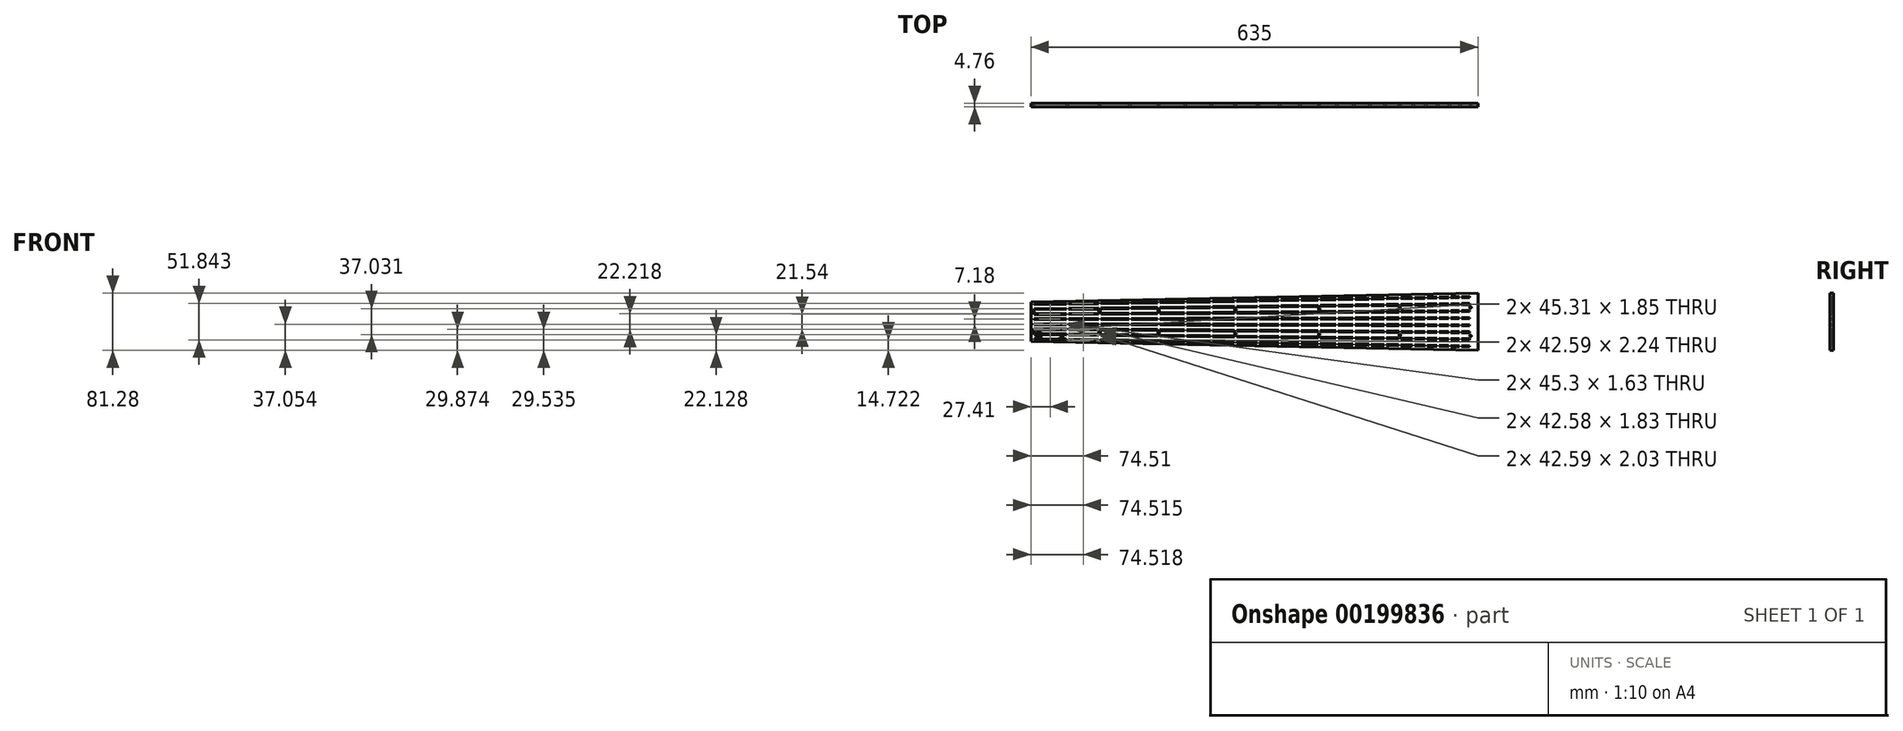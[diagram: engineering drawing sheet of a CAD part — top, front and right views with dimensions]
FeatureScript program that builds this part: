
annotation { "Feature Type Name" : "Feature", "Feature Type Description" : "" }
export const myFeature = defineFeature(function(context is Context, id is Id, definition is map)
    precondition{}
    {
        {
            var Q0;
            Q0=qCreatedBy(makeId("Front.planeOp"),FACE);
            var sketch = newSketch(context, id + "F0", { "sketchPlane" : qUnion([Q0])});
            skLineSegment(sketch, "E0", {"start": v(0, 3.52) * mm, "end": v(648.16, -7.37) * mm, "construction": true});
            skLineSegment(sketch, "E1", {"start": v(0, 4.29) * mm, "end": v(642.9, -6.52) * mm, "construction": true});
            skLineSegment(sketch, "E2", {"start": v(4.76, 3.44) * mm, "end": v(4.77, 4.2) * mm});
            skLineSegment(sketch, "E3", {"start": v(4.77, 4.2) * mm, "end": v(50.06, 3.45) * mm});
            skLineSegment(sketch, "E4", {"start": v(50.06, 3.45) * mm, "end": v(50.05, 2.68) * mm});
            skLineSegment(sketch, "E5", {"start": v(53.23, 2.63) * mm, "end": v(53.24, 3.4) * mm});
            skLineSegment(sketch, "E6", {"start": v(53.24, 3.4) * mm, "end": v(95.8, 2.68) * mm});
            skLineSegment(sketch, "E7", {"start": v(95.8, 2.68) * mm, "end": v(95.8, 1.91) * mm});
            skLineSegment(sketch, "E8", {"start": v(98.97, 1.86) * mm, "end": v(98.98, 2.62) * mm});
            skLineSegment(sketch, "E9", {"start": v(98.98, 2.62) * mm, "end": v(138.98, 1.95) * mm});
            skLineSegment(sketch, "E10", {"start": v(138.98, 1.95) * mm, "end": v(138.97, 1.19) * mm});
            skLineSegment(sketch, "E11", {"start": v(142.14, 1.14) * mm, "end": v(142.16, 1.9) * mm});
            skLineSegment(sketch, "E12", {"start": v(142.16, 1.9) * mm, "end": v(179.73, 1.27) * mm});
            skLineSegment(sketch, "E13", {"start": v(179.73, 1.27) * mm, "end": v(179.72, 0.5) * mm});
            skLineSegment(sketch, "E14", {"start": v(182.89, 0.45) * mm, "end": v(182.9, 1.21) * mm});
            skLineSegment(sketch, "E15", {"start": v(182.9, 1.21) * mm, "end": v(218.2, 0.62) * mm, "construction": true});
            skLineSegment(sketch, "E16", {"start": v(218.2, 0.62) * mm, "end": v(218.19, -0.14) * mm});
            skLineSegment(sketch, "E17", {"start": v(221.36, -0.2) * mm, "end": v(221.38, 0.57) * mm});
            skLineSegment(sketch, "E18", {"start": v(221.38, 0.57) * mm, "end": v(254.5, 0.01) * mm});
            skLineSegment(sketch, "E19", {"start": v(254.5, 0.01) * mm, "end": v(254.5, -0.75) * mm});
            skLineSegment(sketch, "E20", {"start": v(257.67, -0.8) * mm, "end": v(257.68, -0.04) * mm});
            skLineSegment(sketch, "E21", {"start": v(257.68, -0.04) * mm, "end": v(288.78, -0.57) * mm});
            skLineSegment(sketch, "E22", {"start": v(288.78, -0.57) * mm, "end": v(288.76, -1.33) * mm});
            skLineSegment(sketch, "E23", {"start": v(291.94, -1.38) * mm, "end": v(291.95, -0.62) * mm});
            skLineSegment(sketch, "E24", {"start": v(291.95, -0.62) * mm, "end": v(321.12, -1.1) * mm});
            skLineSegment(sketch, "E25", {"start": v(321.12, -1.1) * mm, "end": v(321.1, -1.87) * mm});
            skLineSegment(sketch, "E26", {"start": v(324.28, -1.92) * mm, "end": v(324.3, -1.16) * mm});
            skLineSegment(sketch, "E27", {"start": v(324.3, -1.16) * mm, "end": v(351.65, -1.62) * mm});
            skLineSegment(sketch, "E28", {"start": v(351.65, -1.62) * mm, "end": v(351.64, -2.38) * mm});
            skLineSegment(sketch, "E29", {"start": v(182.9, 1.21) * mm, "end": v(218.2, 0.62) * mm});
            skLineSegment(sketch, "E30", {"start": v(354.81, -2.44) * mm, "end": v(354.83, -1.68) * mm});
            skLineSegment(sketch, "E31", {"start": v(354.83, -1.68) * mm, "end": v(380.47, -2.1) * mm});
            skLineSegment(sketch, "E32", {"start": v(380.47, -2.1) * mm, "end": v(380.45, -2.87) * mm});
            skLineSegment(sketch, "E33", {"start": v(383.63, -2.92) * mm, "end": v(383.64, -2.16) * mm});
            skLineSegment(sketch, "E34", {"start": v(383.64, -2.16) * mm, "end": v(407.67, -2.56) * mm});
            skLineSegment(sketch, "E35", {"start": v(407.67, -2.56) * mm, "end": v(407.65, -3.33) * mm});
            skLineSegment(sketch, "E36", {"start": v(410.83, -3.38) * mm, "end": v(410.84, -2.62) * mm});
            skLineSegment(sketch, "E37", {"start": v(410.84, -2.62) * mm, "end": v(433.34, -3) * mm});
            skLineSegment(sketch, "E38", {"start": v(433.34, -3) * mm, "end": v(433.33, -3.76) * mm});
            skLineSegment(sketch, "E39", {"start": v(436.5, -3.8) * mm, "end": v(436.51, -3.05) * mm});
            skLineSegment(sketch, "E40", {"start": v(436.51, -3.05) * mm, "end": v(457.57, -3.4) * mm});
            skLineSegment(sketch, "E41", {"start": v(457.57, -3.4) * mm, "end": v(457.56, -4.16) * mm});
            skLineSegment(sketch, "E42", {"start": v(460.73, -4.22) * mm, "end": v(460.75, -3.46) * mm});
            skLineSegment(sketch, "E43", {"start": v(460.75, -3.46) * mm, "end": v(480.44, -3.79) * mm});
            skLineSegment(sketch, "E44", {"start": v(480.44, -3.79) * mm, "end": v(480.43, -4.55) * mm});
            skLineSegment(sketch, "E45", {"start": v(483.6, -4.6) * mm, "end": v(483.62, -3.84) * mm});
            skLineSegment(sketch, "E46", {"start": v(483.62, -3.84) * mm, "end": v(502.03, -4.15) * mm});
            skLineSegment(sketch, "E47", {"start": v(502.03, -4.15) * mm, "end": v(502.02, -4.91) * mm});
            skLineSegment(sketch, "E48", {"start": v(505.2, -4.96) * mm, "end": v(505.2, -4.2) * mm});
            skLineSegment(sketch, "E49", {"start": v(505.2, -4.2) * mm, "end": v(522.4, -4.5) * mm});
            skLineSegment(sketch, "E50", {"start": v(522.4, -4.5) * mm, "end": v(522.4, -5.25) * mm});
            skLineSegment(sketch, "E51", {"start": v(525.57, -5.3) * mm, "end": v(525.58, -4.54) * mm});
            skLineSegment(sketch, "E52", {"start": v(525.58, -4.54) * mm, "end": v(541.64, -4.81) * mm});
            skLineSegment(sketch, "E53", {"start": v(541.64, -4.81) * mm, "end": v(541.63, -5.58) * mm});
            skLineSegment(sketch, "E54", {"start": v(544.8, -5.63) * mm, "end": v(544.81, -4.87) * mm});
            skLineSegment(sketch, "E55", {"start": v(544.81, -4.87) * mm, "end": v(559.8, -5.12) * mm});
            skLineSegment(sketch, "E56", {"start": v(559.8, -5.12) * mm, "end": v(559.78, -5.88) * mm});
            skLineSegment(sketch, "E57", {"start": v(562.95, -5.93) * mm, "end": v(562.97, -5.17) * mm});
            skLineSegment(sketch, "E58", {"start": v(562.97, -5.17) * mm, "end": v(576.93, -5.4) * mm});
            skLineSegment(sketch, "E59", {"start": v(576.93, -5.4) * mm, "end": v(576.91, -6.17) * mm});
            skLineSegment(sketch, "E60", {"start": v(580.09, -6.22) * mm, "end": v(580.1, -5.46) * mm});
            skLineSegment(sketch, "E61", {"start": v(580.1, -5.46) * mm, "end": v(593.1, -5.68) * mm});
            skLineSegment(sketch, "E62", {"start": v(593.1, -5.68) * mm, "end": v(593.09, -6.44) * mm});
            skLineSegment(sketch, "E63", {"start": v(596.26, -6.5) * mm, "end": v(596.27, -5.73) * mm});
            skLineSegment(sketch, "E64", {"start": v(596.27, -5.73) * mm, "end": v(608.36, -5.94) * mm});
            skLineSegment(sketch, "E65", {"start": v(608.36, -5.94) * mm, "end": v(608.35, -6.7) * mm});
            skLineSegment(sketch, "E66", {"start": v(611.53, -6.75) * mm, "end": v(611.54, -5.99) * mm});
            skLineSegment(sketch, "E67", {"start": v(611.54, -5.99) * mm, "end": v(622.77, -6.18) * mm});
            skLineSegment(sketch, "E68", {"start": v(622.77, -6.18) * mm, "end": v(622.76, -6.94) * mm});
            skLineSegment(sketch, "E69.MirrorCS", {"start": v(182.89, 0.45) * mm, "end": v(182.88, -0.31) * mm});
            skLineSegment(sketch, "E70.MirrorCS", {"start": v(608.34, -7.46) * mm, "end": v(608.35, -6.7) * mm});
            skLineSegment(sketch, "E71.MirrorCS", {"start": v(221.36, -0.2) * mm, "end": v(221.35, -0.96) * mm});
            skLineSegment(sketch, "E72.MirrorCS", {"start": v(559.77, -6.64) * mm, "end": v(559.78, -5.88) * mm});
            skLineSegment(sketch, "E73.MirrorCS", {"start": v(218.18, -0.9) * mm, "end": v(218.19, -0.14) * mm});
            skLineSegment(sketch, "E74.MirrorCS", {"start": v(291.94, -1.38) * mm, "end": v(291.92, -2.14) * mm});
            skLineSegment(sketch, "E75.MirrorCS", {"start": v(95.78, 1.15) * mm, "end": v(95.8, 1.91) * mm});
            skLineSegment(sketch, "E76.MirrorCS", {"start": v(50.04, 1.92) * mm, "end": v(50.05, 2.68) * mm});
            skLineSegment(sketch, "E77.MirrorCS", {"start": v(611.53, -6.75) * mm, "end": v(611.51, -7.51) * mm});
            skLineSegment(sketch, "E78.MirrorCS", {"start": v(596.26, -6.5) * mm, "end": v(596.25, -7.26) * mm});
            skLineSegment(sketch, "E79.MirrorCS", {"start": v(324.28, -1.92) * mm, "end": v(324.27, -2.69) * mm});
            skLineSegment(sketch, "E80.MirrorCS", {"start": v(580.09, -6.22) * mm, "end": v(580.08, -6.98) * mm});
            skLineSegment(sketch, "E81.MirrorCS", {"start": v(480.42, -5.3) * mm, "end": v(480.43, -4.55) * mm});
            skLineSegment(sketch, "E82.MirrorCS", {"start": v(407.64, -4.09) * mm, "end": v(407.65, -3.33) * mm});
            skLineSegment(sketch, "E83.MirrorCS", {"start": v(593.07, -7.2) * mm, "end": v(593.09, -6.44) * mm});
            skLineSegment(sketch, "E84.MirrorCS", {"start": v(483.6, -4.6) * mm, "end": v(483.6, -5.36) * mm});
            skLineSegment(sketch, "E85.MirrorCS", {"start": v(580.08, -6.98) * mm, "end": v(593.07, -7.2) * mm});
            skLineSegment(sketch, "E86.MirrorCS", {"start": v(522.38, -6.01) * mm, "end": v(522.4, -5.25) * mm});
            skLineSegment(sketch, "E87.MirrorCS", {"start": v(321.1, -2.63) * mm, "end": v(321.1, -1.87) * mm});
            skLineSegment(sketch, "E88.MirrorCS", {"start": v(457.55, -4.93) * mm, "end": v(457.56, -4.16) * mm});
            skLineSegment(sketch, "E89.MirrorCS", {"start": v(562.95, -5.93) * mm, "end": v(562.94, -6.7) * mm});
            skLineSegment(sketch, "E90.MirrorCS", {"start": v(383.63, -2.92) * mm, "end": v(383.62, -3.68) * mm});
            skLineSegment(sketch, "E91.MirrorCS", {"start": v(380.44, -3.63) * mm, "end": v(380.45, -2.87) * mm});
            skLineSegment(sketch, "E92.MirrorCS", {"start": v(505.2, -4.96) * mm, "end": v(505.18, -5.73) * mm});
            skLineSegment(sketch, "E93.MirrorCS", {"start": v(596.25, -7.26) * mm, "end": v(608.34, -7.46) * mm});
            skLineSegment(sketch, "E94.MirrorCS", {"start": v(544.79, -6.4) * mm, "end": v(559.77, -6.64) * mm});
            skLineSegment(sketch, "E95.MirrorCS", {"start": v(142.14, 1.14) * mm, "end": v(142.13, 0.37) * mm});
            skLineSegment(sketch, "E96.MirrorCS", {"start": v(138.96, 0.43) * mm, "end": v(138.97, 1.19) * mm});
            skLineSegment(sketch, "E97.MirrorCS", {"start": v(98.97, 1.86) * mm, "end": v(98.96, 1.1) * mm});
            skLineSegment(sketch, "E98.MirrorCS", {"start": v(53.23, 2.63) * mm, "end": v(53.21, 1.87) * mm});
            skLineSegment(sketch, "E99.MirrorCS", {"start": v(4.76, 3.44) * mm, "end": v(4.75, 2.68) * mm});
            skLineSegment(sketch, "E100.MirrorCS", {"start": v(179.7, -0.26) * mm, "end": v(179.72, 0.5) * mm});
            skLineSegment(sketch, "E101.MirrorCS", {"start": v(433.31, -4.52) * mm, "end": v(433.33, -3.76) * mm});
            skLineSegment(sketch, "E102.MirrorCS", {"start": v(544.8, -5.63) * mm, "end": v(544.79, -6.4) * mm});
            skLineSegment(sketch, "E103.MirrorCS", {"start": v(502, -5.67) * mm, "end": v(502.02, -4.91) * mm});
            skLineSegment(sketch, "E104.MirrorCS", {"start": v(288.75, -2.09) * mm, "end": v(288.76, -1.33) * mm});
            skLineSegment(sketch, "E105.MirrorCS", {"start": v(562.94, -6.7) * mm, "end": v(576.9, -6.93) * mm});
            skLineSegment(sketch, "E106.MirrorCS", {"start": v(254.48, -1.51) * mm, "end": v(254.5, -0.75) * mm});
            skLineSegment(sketch, "E107.MirrorCS", {"start": v(611.51, -7.51) * mm, "end": v(622.75, -7.7) * mm});
            skLineSegment(sketch, "E108.MirrorCS", {"start": v(525.57, -5.3) * mm, "end": v(525.56, -6.07) * mm});
            skLineSegment(sketch, "E109.MirrorCS", {"start": v(351.63, -3.15) * mm, "end": v(351.64, -2.38) * mm});
            skLineSegment(sketch, "E110.MirrorCS", {"start": v(410.83, -3.38) * mm, "end": v(410.82, -4.14) * mm});
            skLineSegment(sketch, "E111.MirrorCS", {"start": v(576.9, -6.93) * mm, "end": v(576.91, -6.17) * mm});
            skLineSegment(sketch, "E112.MirrorCS", {"start": v(257.67, -0.8) * mm, "end": v(257.66, -1.57) * mm});
            skLineSegment(sketch, "E113.MirrorCS", {"start": v(622.75, -7.7) * mm, "end": v(622.76, -6.94) * mm});
            skLineSegment(sketch, "E114.MirrorCS", {"start": v(354.81, -2.44) * mm, "end": v(354.8, -3.2) * mm});
            skLineSegment(sketch, "E115.MirrorCS", {"start": v(505.18, -5.73) * mm, "end": v(522.38, -6.01) * mm});
            skLineSegment(sketch, "E116.MirrorCS", {"start": v(436.5, -3.8) * mm, "end": v(436.49, -4.57) * mm});
            skLineSegment(sketch, "E117.MirrorCS", {"start": v(182.88, -0.31) * mm, "end": v(218.18, -0.9) * mm, "construction": true});
            skLineSegment(sketch, "E118.MirrorCS", {"start": v(460.73, -4.22) * mm, "end": v(460.72, -4.98) * mm});
            skLineSegment(sketch, "E119.MirrorCS", {"start": v(541.61, -6.34) * mm, "end": v(541.63, -5.58) * mm});
            skLineSegment(sketch, "E120.MirrorCS", {"start": v(525.56, -6.07) * mm, "end": v(541.61, -6.34) * mm});
            skLineSegment(sketch, "E121.MirrorCS", {"start": v(221.35, -0.96) * mm, "end": v(254.48, -1.51) * mm});
            skLineSegment(sketch, "E122.MirrorCS", {"start": v(383.62, -3.68) * mm, "end": v(407.64, -4.09) * mm});
            skLineSegment(sketch, "E123.MirrorCS", {"start": v(291.92, -2.14) * mm, "end": v(321.1, -2.63) * mm});
            skLineSegment(sketch, "E124.MirrorCS", {"start": v(436.49, -4.57) * mm, "end": v(457.55, -4.93) * mm});
            skLineSegment(sketch, "E125.MirrorCS", {"start": v(142.13, 0.37) * mm, "end": v(179.7, -0.26) * mm});
            skLineSegment(sketch, "E126.MirrorCS", {"start": v(53.21, 1.87) * mm, "end": v(95.78, 1.15) * mm});
            skLineSegment(sketch, "E127.MirrorCS", {"start": v(4.75, 2.68) * mm, "end": v(50.04, 1.92) * mm});
            skLineSegment(sketch, "E128.MirrorCS", {"start": v(354.8, -3.2) * mm, "end": v(380.44, -3.63) * mm});
            skLineSegment(sketch, "E129.MirrorCS", {"start": v(257.66, -1.57) * mm, "end": v(288.75, -2.09) * mm});
            skLineSegment(sketch, "E130.MirrorCS", {"start": v(483.6, -5.36) * mm, "end": v(502, -5.67) * mm});
            skLineSegment(sketch, "E131.MirrorCS", {"start": v(410.82, -4.14) * mm, "end": v(433.31, -4.52) * mm});
            skLineSegment(sketch, "E132.MirrorCS", {"start": v(182.88, -0.31) * mm, "end": v(218.18, -0.9) * mm});
            skLineSegment(sketch, "E133.MirrorCS", {"start": v(460.72, -4.98) * mm, "end": v(480.42, -5.3) * mm});
            skLineSegment(sketch, "E134.MirrorCS", {"start": v(324.27, -2.69) * mm, "end": v(351.63, -3.15) * mm});
            skLineSegment(sketch, "E135.MirrorCS", {"start": v(98.96, 1.1) * mm, "end": v(138.96, 0.43) * mm});
            skLineSegment(sketch, "E136", {"start": v(-33.04, 0) * mm, "end": v(118.54, 0) * mm, "construction": true});
            skLineSegment(sketch, "E137", {"start": v(0, 10.57) * mm, "end": v(648.2, 2.8) * mm, "construction": true});
            skLineSegment(sketch, "E138", {"start": v(0, 11.33) * mm, "end": v(642.94, 3.62) * mm, "construction": true});
            skLineSegment(sketch, "E139", {"start": v(4.76, 10.52) * mm, "end": v(4.77, 11.28) * mm});
            skLineSegment(sketch, "E140", {"start": v(4.77, 11.28) * mm, "end": v(50.06, 10.73) * mm});
            skLineSegment(sketch, "E141", {"start": v(50.06, 10.73) * mm, "end": v(50.05, 9.97) * mm});
            skLineSegment(sketch, "E142", {"start": v(53.23, 9.93) * mm, "end": v(53.24, 10.7) * mm});
            skLineSegment(sketch, "E143", {"start": v(53.24, 10.7) * mm, "end": v(95.8, 10.19) * mm});
            skLineSegment(sketch, "E144", {"start": v(95.8, 10.19) * mm, "end": v(95.8, 9.42) * mm});
            skLineSegment(sketch, "E145", {"start": v(98.97, 9.38) * mm, "end": v(98.98, 10.15) * mm});
            skLineSegment(sketch, "E146", {"start": v(98.98, 10.15) * mm, "end": v(138.99, 9.67) * mm});
            skLineSegment(sketch, "E147", {"start": v(138.99, 9.67) * mm, "end": v(138.98, 8.9) * mm});
            skLineSegment(sketch, "E148", {"start": v(142.15, 8.87) * mm, "end": v(142.16, 9.63) * mm});
            skLineSegment(sketch, "E149", {"start": v(142.16, 9.63) * mm, "end": v(179.74, 9.18) * mm});
            skLineSegment(sketch, "E150", {"start": v(179.74, 9.18) * mm, "end": v(179.73, 8.42) * mm});
            skLineSegment(sketch, "E151", {"start": v(182.9, 8.38) * mm, "end": v(182.91, 9.14) * mm});
            skLineSegment(sketch, "E152", {"start": v(182.91, 9.14) * mm, "end": v(218.21, 8.72) * mm, "construction": true});
            skLineSegment(sketch, "E153", {"start": v(218.21, 8.72) * mm, "end": v(218.2, 7.95) * mm});
            skLineSegment(sketch, "E154", {"start": v(221.38, 7.92) * mm, "end": v(221.39, 8.68) * mm});
            skLineSegment(sketch, "E155", {"start": v(221.39, 8.68) * mm, "end": v(254.52, 8.28) * mm});
            skLineSegment(sketch, "E156", {"start": v(254.52, 8.28) * mm, "end": v(254.51, 7.52) * mm});
            skLineSegment(sketch, "E157", {"start": v(257.69, 7.48) * mm, "end": v(257.7, 8.24) * mm});
            skLineSegment(sketch, "E158", {"start": v(257.7, 8.24) * mm, "end": v(288.8, 7.87) * mm});
            skLineSegment(sketch, "E159", {"start": v(288.8, 7.87) * mm, "end": v(288.78, 7.1) * mm});
            skLineSegment(sketch, "E160", {"start": v(291.96, 7.07) * mm, "end": v(291.97, 7.83) * mm});
            skLineSegment(sketch, "E161", {"start": v(291.97, 7.83) * mm, "end": v(321.14, 7.48) * mm});
            skLineSegment(sketch, "E162", {"start": v(321.14, 7.48) * mm, "end": v(321.13, 6.72) * mm});
            skLineSegment(sketch, "E163", {"start": v(324.3, 6.68) * mm, "end": v(324.31, 7.44) * mm});
            skLineSegment(sketch, "E164", {"start": v(324.31, 7.44) * mm, "end": v(351.67, 7.11) * mm});
            skLineSegment(sketch, "E165", {"start": v(351.67, 7.11) * mm, "end": v(351.66, 6.35) * mm});
            skLineSegment(sketch, "E166", {"start": v(182.91, 9.14) * mm, "end": v(218.21, 8.72) * mm});
            skLineSegment(sketch, "E167", {"start": v(354.84, 6.31) * mm, "end": v(354.85, 7.08) * mm});
            skLineSegment(sketch, "E168", {"start": v(354.85, 7.08) * mm, "end": v(380.5, 6.77) * mm});
            skLineSegment(sketch, "E169", {"start": v(380.5, 6.77) * mm, "end": v(380.48, 6) * mm});
            skLineSegment(sketch, "E170", {"start": v(383.66, 5.97) * mm, "end": v(383.66, 6.73) * mm});
            skLineSegment(sketch, "E171", {"start": v(383.66, 6.73) * mm, "end": v(407.7, 6.44) * mm});
            skLineSegment(sketch, "E172", {"start": v(407.7, 6.44) * mm, "end": v(407.68, 5.68) * mm});
            skLineSegment(sketch, "E173", {"start": v(410.86, 5.64) * mm, "end": v(410.87, 6.4) * mm});
            skLineSegment(sketch, "E174", {"start": v(410.87, 6.4) * mm, "end": v(433.37, 6.13) * mm});
            skLineSegment(sketch, "E175", {"start": v(433.37, 6.13) * mm, "end": v(433.36, 5.37) * mm});
            skLineSegment(sketch, "E176", {"start": v(436.53, 5.33) * mm, "end": v(436.54, 6.1) * mm});
            skLineSegment(sketch, "E177", {"start": v(436.54, 6.1) * mm, "end": v(457.6, 5.84) * mm});
            skLineSegment(sketch, "E178", {"start": v(457.6, 5.84) * mm, "end": v(457.59, 5.08) * mm});
            skLineSegment(sketch, "E179", {"start": v(460.76, 5.04) * mm, "end": v(460.77, 5.8) * mm});
            skLineSegment(sketch, "E180", {"start": v(460.77, 5.8) * mm, "end": v(480.47, 5.57) * mm});
            skLineSegment(sketch, "E181", {"start": v(480.47, 5.57) * mm, "end": v(480.46, 4.8) * mm});
            skLineSegment(sketch, "E182", {"start": v(483.64, 4.77) * mm, "end": v(483.65, 5.53) * mm});
            skLineSegment(sketch, "E183", {"start": v(483.65, 5.53) * mm, "end": v(502.06, 5.3) * mm});
            skLineSegment(sketch, "E184", {"start": v(502.06, 5.3) * mm, "end": v(502.05, 4.55) * mm});
            skLineSegment(sketch, "E185", {"start": v(505.23, 4.5) * mm, "end": v(505.24, 5.27) * mm});
            skLineSegment(sketch, "E186", {"start": v(505.24, 5.27) * mm, "end": v(522.44, 5.07) * mm});
            skLineSegment(sketch, "E187", {"start": v(522.44, 5.07) * mm, "end": v(522.43, 4.3) * mm});
            skLineSegment(sketch, "E188", {"start": v(525.6, 4.27) * mm, "end": v(525.61, 5.03) * mm});
            skLineSegment(sketch, "E189", {"start": v(525.61, 5.03) * mm, "end": v(541.67, 4.83) * mm});
            skLineSegment(sketch, "E190", {"start": v(541.67, 4.83) * mm, "end": v(541.66, 4.07) * mm});
            skLineSegment(sketch, "E191", {"start": v(544.84, 4.03) * mm, "end": v(544.85, 4.8) * mm});
            skLineSegment(sketch, "E192", {"start": v(544.85, 4.8) * mm, "end": v(559.83, 4.62) * mm});
            skLineSegment(sketch, "E193", {"start": v(559.83, 4.62) * mm, "end": v(559.82, 3.85) * mm});
            skLineSegment(sketch, "E194", {"start": v(563, 3.82) * mm, "end": v(563, 4.58) * mm});
            skLineSegment(sketch, "E195", {"start": v(563, 4.58) * mm, "end": v(576.96, 4.41) * mm});
            skLineSegment(sketch, "E196", {"start": v(576.96, 4.41) * mm, "end": v(576.95, 3.65) * mm});
            skLineSegment(sketch, "E197", {"start": v(580.13, 3.61) * mm, "end": v(580.14, 4.37) * mm});
            skLineSegment(sketch, "E198", {"start": v(580.14, 4.37) * mm, "end": v(593.14, 4.22) * mm});
            skLineSegment(sketch, "E199", {"start": v(593.14, 4.22) * mm, "end": v(593.13, 3.45) * mm});
            skLineSegment(sketch, "E200", {"start": v(596.3, 3.42) * mm, "end": v(596.31, 4.18) * mm});
            skLineSegment(sketch, "E201", {"start": v(596.31, 4.18) * mm, "end": v(608.4, 4.03) * mm});
            skLineSegment(sketch, "E202", {"start": v(608.4, 4.03) * mm, "end": v(608.4, 3.27) * mm});
            skLineSegment(sketch, "E203", {"start": v(611.57, 3.23) * mm, "end": v(611.58, 4) * mm});
            skLineSegment(sketch, "E204", {"start": v(611.58, 4) * mm, "end": v(622.81, 3.86) * mm});
            skLineSegment(sketch, "E205", {"start": v(622.81, 3.86) * mm, "end": v(622.8, 3.1) * mm});
            skLineSegment(sketch, "E206.MirrorCS", {"start": v(182.9, 8.38) * mm, "end": v(182.9, 7.62) * mm});
            skLineSegment(sketch, "E207.MirrorCS", {"start": v(608.38, 2.5) * mm, "end": v(608.4, 3.27) * mm});
            skLineSegment(sketch, "E208.MirrorCS", {"start": v(221.38, 7.92) * mm, "end": v(221.37, 7.15) * mm});
            skLineSegment(sketch, "E209.MirrorCS", {"start": v(559.8, 3.1) * mm, "end": v(559.82, 3.85) * mm});
            skLineSegment(sketch, "E210.MirrorCS", {"start": v(218.2, 7.2) * mm, "end": v(218.2, 7.95) * mm});
            skLineSegment(sketch, "E211.MirrorCS", {"start": v(291.96, 7.07) * mm, "end": v(291.95, 6.3) * mm});
            skLineSegment(sketch, "E212.MirrorCS", {"start": v(95.8, 8.66) * mm, "end": v(95.8, 9.42) * mm});
            skLineSegment(sketch, "E213.MirrorCS", {"start": v(50.05, 9.21) * mm, "end": v(50.05, 9.97) * mm});
            skLineSegment(sketch, "E214.MirrorCS", {"start": v(611.57, 3.23) * mm, "end": v(611.56, 2.47) * mm});
            skLineSegment(sketch, "E215.MirrorCS", {"start": v(596.3, 3.42) * mm, "end": v(596.3, 2.65) * mm});
            skLineSegment(sketch, "E216.MirrorCS", {"start": v(324.3, 6.68) * mm, "end": v(324.3, 5.92) * mm});
            skLineSegment(sketch, "E217.MirrorCS", {"start": v(580.13, 3.61) * mm, "end": v(580.12, 2.85) * mm});
            skLineSegment(sketch, "E218.MirrorCS", {"start": v(480.45, 4.05) * mm, "end": v(480.46, 4.8) * mm});
            skLineSegment(sketch, "E219.MirrorCS", {"start": v(407.67, 4.92) * mm, "end": v(407.68, 5.68) * mm});
            skLineSegment(sketch, "E220.MirrorCS", {"start": v(593.12, 2.7) * mm, "end": v(593.13, 3.45) * mm});
            skLineSegment(sketch, "E221.MirrorCS", {"start": v(483.64, 4.77) * mm, "end": v(483.63, 4) * mm});
            skLineSegment(sketch, "E222.MirrorCS", {"start": v(580.12, 2.85) * mm, "end": v(593.12, 2.7) * mm});
            skLineSegment(sketch, "E223.MirrorCS", {"start": v(522.42, 3.54) * mm, "end": v(522.43, 4.3) * mm});
            skLineSegment(sketch, "E224.MirrorCS", {"start": v(321.12, 5.96) * mm, "end": v(321.13, 6.72) * mm});
            skLineSegment(sketch, "E225.MirrorCS", {"start": v(457.58, 4.32) * mm, "end": v(457.59, 5.08) * mm});
            skLineSegment(sketch, "E226.MirrorCS", {"start": v(563, 3.82) * mm, "end": v(562.98, 3.05) * mm});
            skLineSegment(sketch, "E227.MirrorCS", {"start": v(383.66, 5.97) * mm, "end": v(383.65, 5.2) * mm});
            skLineSegment(sketch, "E228.MirrorCS", {"start": v(380.47, 5.24) * mm, "end": v(380.48, 6) * mm});
            skLineSegment(sketch, "E229.MirrorCS", {"start": v(505.23, 4.5) * mm, "end": v(505.22, 3.75) * mm});
            skLineSegment(sketch, "E230.MirrorCS", {"start": v(596.3, 2.65) * mm, "end": v(608.38, 2.5) * mm});
            skLineSegment(sketch, "E231.MirrorCS", {"start": v(544.83, 3.27) * mm, "end": v(559.8, 3.1) * mm});
            skLineSegment(sketch, "E232.MirrorCS", {"start": v(142.15, 8.87) * mm, "end": v(142.15, 8.1) * mm});
            skLineSegment(sketch, "E233.MirrorCS", {"start": v(138.97, 8.14) * mm, "end": v(138.98, 8.9) * mm});
            skLineSegment(sketch, "E234.MirrorCS", {"start": v(98.97, 9.38) * mm, "end": v(98.97, 8.62) * mm});
            skLineSegment(sketch, "E235.MirrorCS", {"start": v(53.23, 9.93) * mm, "end": v(53.22, 9.17) * mm});
            skLineSegment(sketch, "E236.MirrorCS", {"start": v(4.76, 10.52) * mm, "end": v(4.75, 9.75) * mm});
            skLineSegment(sketch, "E237.MirrorCS", {"start": v(179.72, 7.65) * mm, "end": v(179.73, 8.42) * mm});
            skLineSegment(sketch, "E238.MirrorCS", {"start": v(433.35, 4.61) * mm, "end": v(433.36, 5.37) * mm});
            skLineSegment(sketch, "E239.MirrorCS", {"start": v(544.84, 4.03) * mm, "end": v(544.83, 3.27) * mm});
            skLineSegment(sketch, "E240.MirrorCS", {"start": v(502.04, 3.79) * mm, "end": v(502.05, 4.55) * mm});
            skLineSegment(sketch, "E241.MirrorCS", {"start": v(288.77, 6.35) * mm, "end": v(288.78, 7.1) * mm});
            skLineSegment(sketch, "E242.MirrorCS", {"start": v(562.98, 3.05) * mm, "end": v(576.94, 2.89) * mm});
            skLineSegment(sketch, "E243.MirrorCS", {"start": v(254.5, 6.76) * mm, "end": v(254.51, 7.52) * mm});
            skLineSegment(sketch, "E244.MirrorCS", {"start": v(611.56, 2.47) * mm, "end": v(622.8, 2.34) * mm});
            skLineSegment(sketch, "E245.MirrorCS", {"start": v(525.6, 4.27) * mm, "end": v(525.6, 3.5) * mm});
            skLineSegment(sketch, "E246.MirrorCS", {"start": v(351.65, 5.6) * mm, "end": v(351.66, 6.35) * mm});
            skLineSegment(sketch, "E247.MirrorCS", {"start": v(410.86, 5.64) * mm, "end": v(410.85, 4.88) * mm});
            skLineSegment(sketch, "E248.MirrorCS", {"start": v(576.94, 2.89) * mm, "end": v(576.95, 3.65) * mm});
            skLineSegment(sketch, "E249.MirrorCS", {"start": v(257.69, 7.48) * mm, "end": v(257.68, 6.72) * mm});
            skLineSegment(sketch, "E250.MirrorCS", {"start": v(622.8, 2.34) * mm, "end": v(622.8, 3.1) * mm});
            skLineSegment(sketch, "E251.MirrorCS", {"start": v(354.84, 6.31) * mm, "end": v(354.83, 5.55) * mm});
            skLineSegment(sketch, "E252.MirrorCS", {"start": v(505.22, 3.75) * mm, "end": v(522.42, 3.54) * mm});
            skLineSegment(sketch, "E253.MirrorCS", {"start": v(436.53, 5.33) * mm, "end": v(436.52, 4.57) * mm});
            skLineSegment(sketch, "E254.MirrorCS", {"start": v(182.9, 7.62) * mm, "end": v(218.2, 7.2) * mm, "construction": true});
            skLineSegment(sketch, "E255.MirrorCS", {"start": v(460.76, 5.04) * mm, "end": v(460.76, 4.28) * mm});
            skLineSegment(sketch, "E256.MirrorCS", {"start": v(541.65, 3.31) * mm, "end": v(541.66, 4.07) * mm});
            skLineSegment(sketch, "E257.MirrorCS", {"start": v(525.6, 3.5) * mm, "end": v(541.65, 3.31) * mm});
            skLineSegment(sketch, "E258.MirrorCS", {"start": v(221.37, 7.15) * mm, "end": v(254.5, 6.76) * mm});
            skLineSegment(sketch, "E259.MirrorCS", {"start": v(383.65, 5.2) * mm, "end": v(407.67, 4.92) * mm});
            skLineSegment(sketch, "E260.MirrorCS", {"start": v(291.95, 6.3) * mm, "end": v(321.12, 5.96) * mm});
            skLineSegment(sketch, "E261.MirrorCS", {"start": v(436.52, 4.57) * mm, "end": v(457.58, 4.32) * mm});
            skLineSegment(sketch, "E262.MirrorCS", {"start": v(142.15, 8.1) * mm, "end": v(179.72, 7.65) * mm});
            skLineSegment(sketch, "E263.MirrorCS", {"start": v(53.22, 9.17) * mm, "end": v(95.8, 8.66) * mm});
            skLineSegment(sketch, "E264.MirrorCS", {"start": v(4.75, 9.75) * mm, "end": v(50.05, 9.21) * mm});
            skLineSegment(sketch, "E265.MirrorCS", {"start": v(354.83, 5.55) * mm, "end": v(380.47, 5.24) * mm});
            skLineSegment(sketch, "E266.MirrorCS", {"start": v(257.68, 6.72) * mm, "end": v(288.77, 6.35) * mm});
            skLineSegment(sketch, "E267.MirrorCS", {"start": v(483.63, 4) * mm, "end": v(502.04, 3.79) * mm});
            skLineSegment(sketch, "E268.MirrorCS", {"start": v(410.85, 4.88) * mm, "end": v(433.35, 4.61) * mm});
            skLineSegment(sketch, "E269.MirrorCS", {"start": v(182.9, 7.62) * mm, "end": v(218.2, 7.2) * mm});
            skLineSegment(sketch, "E270.MirrorCS", {"start": v(460.76, 4.28) * mm, "end": v(480.45, 4.05) * mm});
            skLineSegment(sketch, "E271.MirrorCS", {"start": v(324.3, 5.92) * mm, "end": v(351.65, 5.6) * mm});
            skLineSegment(sketch, "E272.MirrorCS", {"start": v(98.97, 8.62) * mm, "end": v(138.97, 8.14) * mm});
            skLineSegment(sketch, "E273", {"start": v(0, 17.62) * mm, "end": v(648.23, 12.95) * mm, "construction": true});
            skLineSegment(sketch, "E274", {"start": v(0, 18.38) * mm, "end": v(642.97, 13.75) * mm, "construction": true});
            skLineSegment(sketch, "E275", {"start": v(4.76, 17.59) * mm, "end": v(4.77, 18.35) * mm});
            skLineSegment(sketch, "E276", {"start": v(4.77, 18.35) * mm, "end": v(50.06, 18.02) * mm});
            skLineSegment(sketch, "E277", {"start": v(50.06, 18.02) * mm, "end": v(50.06, 17.26) * mm});
            skLineSegment(sketch, "E278", {"start": v(53.23, 17.24) * mm, "end": v(53.24, 18) * mm});
            skLineSegment(sketch, "E279", {"start": v(53.24, 18) * mm, "end": v(95.81, 17.7) * mm});
            skLineSegment(sketch, "E280", {"start": v(95.81, 17.7) * mm, "end": v(95.8, 16.93) * mm});
            skLineSegment(sketch, "E281", {"start": v(98.98, 16.9) * mm, "end": v(98.99, 17.67) * mm});
            skLineSegment(sketch, "E282", {"start": v(98.99, 17.67) * mm, "end": v(139, 17.38) * mm});
            skLineSegment(sketch, "E283", {"start": v(139, 17.38) * mm, "end": v(138.99, 16.62) * mm});
            skLineSegment(sketch, "E284", {"start": v(142.16, 16.6) * mm, "end": v(142.17, 17.36) * mm});
            skLineSegment(sketch, "E285", {"start": v(142.17, 17.36) * mm, "end": v(179.74, 17.09) * mm});
            skLineSegment(sketch, "E286", {"start": v(179.74, 17.09) * mm, "end": v(179.74, 16.33) * mm});
            skLineSegment(sketch, "E287", {"start": v(182.91, 16.3) * mm, "end": v(182.92, 17.07) * mm});
            skLineSegment(sketch, "E288", {"start": v(182.92, 17.07) * mm, "end": v(218.22, 16.81) * mm, "construction": true});
            skLineSegment(sketch, "E289", {"start": v(218.22, 16.81) * mm, "end": v(218.21, 16.05) * mm});
            skLineSegment(sketch, "E290", {"start": v(221.39, 16.03) * mm, "end": v(221.4, 16.79) * mm});
            skLineSegment(sketch, "E291", {"start": v(221.4, 16.79) * mm, "end": v(254.53, 16.55) * mm});
            skLineSegment(sketch, "E292", {"start": v(254.53, 16.55) * mm, "end": v(254.52, 15.79) * mm});
            skLineSegment(sketch, "E293", {"start": v(257.7, 15.77) * mm, "end": v(257.7, 16.53) * mm});
            skLineSegment(sketch, "E294", {"start": v(257.7, 16.53) * mm, "end": v(288.8, 16.3) * mm});
            skLineSegment(sketch, "E295", {"start": v(288.8, 16.3) * mm, "end": v(288.8, 15.54) * mm});
            skLineSegment(sketch, "E296", {"start": v(291.97, 15.52) * mm, "end": v(291.98, 16.28) * mm});
            skLineSegment(sketch, "E297", {"start": v(291.98, 16.28) * mm, "end": v(321.15, 16.07) * mm});
            skLineSegment(sketch, "E298", {"start": v(321.15, 16.07) * mm, "end": v(321.14, 15.3) * mm});
            skLineSegment(sketch, "E299", {"start": v(324.32, 15.29) * mm, "end": v(324.33, 16.05) * mm});
            skLineSegment(sketch, "E300", {"start": v(324.33, 16.05) * mm, "end": v(351.68, 15.85) * mm});
            skLineSegment(sketch, "E301", {"start": v(351.68, 15.85) * mm, "end": v(351.68, 15.09) * mm});
            skLineSegment(sketch, "E302", {"start": v(182.92, 17.07) * mm, "end": v(218.22, 16.81) * mm});
            skLineSegment(sketch, "E303", {"start": v(354.85, 15.07) * mm, "end": v(354.86, 15.83) * mm});
            skLineSegment(sketch, "E304", {"start": v(354.86, 15.83) * mm, "end": v(380.5, 15.64) * mm});
            skLineSegment(sketch, "E305", {"start": v(380.5, 15.64) * mm, "end": v(380.5, 14.88) * mm});
            skLineSegment(sketch, "E306", {"start": v(383.67, 14.86) * mm, "end": v(383.68, 15.62) * mm});
            skLineSegment(sketch, "E307", {"start": v(383.68, 15.62) * mm, "end": v(407.7, 15.45) * mm});
            skLineSegment(sketch, "E308", {"start": v(407.7, 15.45) * mm, "end": v(407.7, 14.69) * mm});
            skLineSegment(sketch, "E309", {"start": v(410.88, 14.66) * mm, "end": v(410.88, 15.42) * mm});
            skLineSegment(sketch, "E310", {"start": v(410.88, 15.42) * mm, "end": v(433.38, 15.26) * mm});
            skLineSegment(sketch, "E311", {"start": v(433.38, 15.26) * mm, "end": v(433.38, 14.5) * mm});
            skLineSegment(sketch, "E312", {"start": v(436.55, 14.48) * mm, "end": v(436.56, 15.24) * mm});
            skLineSegment(sketch, "E313", {"start": v(436.56, 15.24) * mm, "end": v(457.62, 15.09) * mm});
            skLineSegment(sketch, "E314", {"start": v(457.62, 15.09) * mm, "end": v(457.61, 14.33) * mm});
            skLineSegment(sketch, "E315", {"start": v(460.79, 14.3) * mm, "end": v(460.8, 15.07) * mm});
            skLineSegment(sketch, "E316", {"start": v(460.8, 15.07) * mm, "end": v(480.5, 14.92) * mm});
            skLineSegment(sketch, "E317", {"start": v(480.5, 14.92) * mm, "end": v(480.49, 14.16) * mm});
            skLineSegment(sketch, "E318", {"start": v(483.66, 14.14) * mm, "end": v(483.67, 14.9) * mm});
            skLineSegment(sketch, "E319", {"start": v(483.67, 14.9) * mm, "end": v(502.08, 14.77) * mm});
            skLineSegment(sketch, "E320", {"start": v(502.08, 14.77) * mm, "end": v(502.08, 14) * mm});
            skLineSegment(sketch, "E321", {"start": v(505.25, 13.98) * mm, "end": v(505.26, 14.75) * mm});
            skLineSegment(sketch, "E322", {"start": v(505.26, 14.75) * mm, "end": v(522.46, 14.62) * mm});
            skLineSegment(sketch, "E323", {"start": v(522.46, 14.62) * mm, "end": v(522.45, 13.86) * mm});
            skLineSegment(sketch, "E324", {"start": v(525.63, 13.84) * mm, "end": v(525.63, 14.6) * mm});
            skLineSegment(sketch, "E325", {"start": v(525.63, 14.6) * mm, "end": v(541.7, 14.48) * mm});
            skLineSegment(sketch, "E326", {"start": v(541.7, 14.48) * mm, "end": v(541.69, 13.72) * mm});
            skLineSegment(sketch, "E327", {"start": v(544.86, 13.7) * mm, "end": v(544.87, 14.46) * mm});
            skLineSegment(sketch, "E328", {"start": v(544.87, 14.46) * mm, "end": v(559.85, 14.35) * mm});
            skLineSegment(sketch, "E329", {"start": v(559.85, 14.35) * mm, "end": v(559.84, 13.6) * mm});
            skLineSegment(sketch, "E330", {"start": v(563.02, 13.57) * mm, "end": v(563.03, 14.33) * mm});
            skLineSegment(sketch, "E331", {"start": v(563.03, 14.33) * mm, "end": v(576.99, 14.23) * mm});
            skLineSegment(sketch, "E332", {"start": v(576.99, 14.23) * mm, "end": v(576.98, 13.47) * mm});
            skLineSegment(sketch, "E333", {"start": v(580.16, 13.44) * mm, "end": v(580.16, 14.2) * mm});
            skLineSegment(sketch, "E334", {"start": v(580.16, 14.2) * mm, "end": v(593.16, 14.11) * mm});
            skLineSegment(sketch, "E335", {"start": v(593.16, 14.11) * mm, "end": v(593.16, 13.35) * mm});
            skLineSegment(sketch, "E336", {"start": v(596.33, 13.33) * mm, "end": v(596.34, 14.09) * mm});
            skLineSegment(sketch, "E337", {"start": v(596.34, 14.09) * mm, "end": v(608.43, 14) * mm});
            skLineSegment(sketch, "E338", {"start": v(608.43, 14) * mm, "end": v(608.42, 13.24) * mm});
            skLineSegment(sketch, "E339", {"start": v(611.6, 13.22) * mm, "end": v(611.6, 13.98) * mm});
            skLineSegment(sketch, "E340", {"start": v(611.6, 13.98) * mm, "end": v(622.84, 13.9) * mm});
            skLineSegment(sketch, "E341", {"start": v(622.84, 13.9) * mm, "end": v(622.83, 13.14) * mm});
            skLineSegment(sketch, "E342.MirrorCS", {"start": v(182.91, 16.3) * mm, "end": v(182.9, 15.54) * mm});
            skLineSegment(sketch, "E343.MirrorCS", {"start": v(608.42, 12.48) * mm, "end": v(608.42, 13.24) * mm});
            skLineSegment(sketch, "E344.MirrorCS", {"start": v(221.39, 16.03) * mm, "end": v(221.38, 15.27) * mm});
            skLineSegment(sketch, "E345.MirrorCS", {"start": v(559.84, 12.83) * mm, "end": v(559.84, 13.6) * mm});
            skLineSegment(sketch, "E346.MirrorCS", {"start": v(218.2, 15.29) * mm, "end": v(218.21, 16.05) * mm});
            skLineSegment(sketch, "E347.MirrorCS", {"start": v(291.97, 15.52) * mm, "end": v(291.97, 14.76) * mm});
            skLineSegment(sketch, "E348.MirrorCS", {"start": v(95.8, 16.17) * mm, "end": v(95.8, 16.93) * mm});
            skLineSegment(sketch, "E349.MirrorCS", {"start": v(50.05, 16.5) * mm, "end": v(50.06, 17.26) * mm});
            skLineSegment(sketch, "E350.MirrorCS", {"start": v(611.6, 13.22) * mm, "end": v(611.6, 12.46) * mm});
            skLineSegment(sketch, "E351.MirrorCS", {"start": v(596.33, 13.33) * mm, "end": v(596.32, 12.57) * mm});
            skLineSegment(sketch, "E352.MirrorCS", {"start": v(324.32, 15.29) * mm, "end": v(324.31, 14.52) * mm});
            skLineSegment(sketch, "E353.MirrorCS", {"start": v(580.16, 13.44) * mm, "end": v(580.15, 12.68) * mm});
            skLineSegment(sketch, "E354.MirrorCS", {"start": v(480.48, 13.4) * mm, "end": v(480.49, 14.16) * mm});
            skLineSegment(sketch, "E355.MirrorCS", {"start": v(407.7, 13.92) * mm, "end": v(407.7, 14.69) * mm});
            skLineSegment(sketch, "E356.MirrorCS", {"start": v(593.15, 12.59) * mm, "end": v(593.16, 13.35) * mm});
            skLineSegment(sketch, "E357.MirrorCS", {"start": v(483.66, 14.14) * mm, "end": v(483.65, 13.38) * mm});
            skLineSegment(sketch, "E358.MirrorCS", {"start": v(580.15, 12.68) * mm, "end": v(593.15, 12.59) * mm});
            skLineSegment(sketch, "E359.MirrorCS", {"start": v(522.45, 13.1) * mm, "end": v(522.45, 13.86) * mm});
            skLineSegment(sketch, "E360.MirrorCS", {"start": v(321.14, 14.55) * mm, "end": v(321.14, 15.3) * mm});
            skLineSegment(sketch, "E361.MirrorCS", {"start": v(457.6, 13.56) * mm, "end": v(457.61, 14.33) * mm});
            skLineSegment(sketch, "E362.MirrorCS", {"start": v(563.02, 13.57) * mm, "end": v(563.01, 12.8) * mm});
            skLineSegment(sketch, "E363.MirrorCS", {"start": v(383.67, 14.86) * mm, "end": v(383.67, 14.1) * mm});
            skLineSegment(sketch, "E364.MirrorCS", {"start": v(380.5, 14.12) * mm, "end": v(380.5, 14.88) * mm});
            skLineSegment(sketch, "E365.MirrorCS", {"start": v(505.25, 13.98) * mm, "end": v(505.25, 13.22) * mm});
            skLineSegment(sketch, "E366.MirrorCS", {"start": v(596.32, 12.57) * mm, "end": v(608.42, 12.48) * mm});
            skLineSegment(sketch, "E367.MirrorCS", {"start": v(544.86, 12.94) * mm, "end": v(559.84, 12.83) * mm});
            skLineSegment(sketch, "E368.MirrorCS", {"start": v(142.16, 16.6) * mm, "end": v(142.16, 15.84) * mm});
            skLineSegment(sketch, "E369.MirrorCS", {"start": v(138.98, 15.86) * mm, "end": v(138.99, 16.62) * mm});
            skLineSegment(sketch, "E370.MirrorCS", {"start": v(98.98, 16.9) * mm, "end": v(98.97, 16.15) * mm});
            skLineSegment(sketch, "E371.MirrorCS", {"start": v(53.23, 17.24) * mm, "end": v(53.23, 16.48) * mm});
            skLineSegment(sketch, "E372.MirrorCS", {"start": v(4.76, 17.59) * mm, "end": v(4.76, 16.82) * mm});
            skLineSegment(sketch, "E373.MirrorCS", {"start": v(179.73, 15.57) * mm, "end": v(179.74, 16.33) * mm});
            skLineSegment(sketch, "E374.MirrorCS", {"start": v(433.37, 13.74) * mm, "end": v(433.38, 14.5) * mm});
            skLineSegment(sketch, "E375.MirrorCS", {"start": v(544.86, 13.7) * mm, "end": v(544.86, 12.94) * mm});
            skLineSegment(sketch, "E376.MirrorCS", {"start": v(502.07, 13.24) * mm, "end": v(502.08, 14) * mm});
            skLineSegment(sketch, "E377.MirrorCS", {"start": v(288.8, 14.78) * mm, "end": v(288.8, 15.54) * mm});
            skLineSegment(sketch, "E378.MirrorCS", {"start": v(563.01, 12.8) * mm, "end": v(576.98, 12.7) * mm});
            skLineSegment(sketch, "E379.MirrorCS", {"start": v(254.52, 15.03) * mm, "end": v(254.52, 15.79) * mm});
            skLineSegment(sketch, "E380.MirrorCS", {"start": v(611.6, 12.46) * mm, "end": v(622.83, 12.37) * mm});
            skLineSegment(sketch, "E381.MirrorCS", {"start": v(525.63, 13.84) * mm, "end": v(525.62, 13.07) * mm});
            skLineSegment(sketch, "E382.MirrorCS", {"start": v(351.67, 14.33) * mm, "end": v(351.68, 15.09) * mm});
            skLineSegment(sketch, "E383.MirrorCS", {"start": v(410.88, 14.66) * mm, "end": v(410.87, 13.9) * mm});
            skLineSegment(sketch, "E384.MirrorCS", {"start": v(576.98, 12.7) * mm, "end": v(576.98, 13.47) * mm});
            skLineSegment(sketch, "E385.MirrorCS", {"start": v(257.7, 15.77) * mm, "end": v(257.7, 15) * mm});
            skLineSegment(sketch, "E386.MirrorCS", {"start": v(622.83, 12.37) * mm, "end": v(622.83, 13.14) * mm});
            skLineSegment(sketch, "E387.MirrorCS", {"start": v(354.85, 15.07) * mm, "end": v(354.85, 14.3) * mm});
            skLineSegment(sketch, "E388.MirrorCS", {"start": v(505.25, 13.22) * mm, "end": v(522.45, 13.1) * mm});
            skLineSegment(sketch, "E389.MirrorCS", {"start": v(436.55, 14.48) * mm, "end": v(436.55, 13.72) * mm});
            skLineSegment(sketch, "E390.MirrorCS", {"start": v(182.9, 15.54) * mm, "end": v(218.2, 15.29) * mm, "construction": true});
            skLineSegment(sketch, "E391.MirrorCS", {"start": v(460.79, 14.3) * mm, "end": v(460.78, 13.54) * mm});
            skLineSegment(sketch, "E392.MirrorCS", {"start": v(541.68, 12.96) * mm, "end": v(541.69, 13.72) * mm});
            skLineSegment(sketch, "E393.MirrorCS", {"start": v(525.62, 13.07) * mm, "end": v(541.68, 12.96) * mm});
            skLineSegment(sketch, "E394.MirrorCS", {"start": v(221.38, 15.27) * mm, "end": v(254.52, 15.03) * mm});
            skLineSegment(sketch, "E395.MirrorCS", {"start": v(383.67, 14.1) * mm, "end": v(407.7, 13.92) * mm});
            skLineSegment(sketch, "E396.MirrorCS", {"start": v(291.97, 14.76) * mm, "end": v(321.14, 14.55) * mm});
            skLineSegment(sketch, "E397.MirrorCS", {"start": v(436.55, 13.72) * mm, "end": v(457.6, 13.56) * mm});
            skLineSegment(sketch, "E398.MirrorCS", {"start": v(142.16, 15.84) * mm, "end": v(179.73, 15.57) * mm});
            skLineSegment(sketch, "E399.MirrorCS", {"start": v(53.23, 16.48) * mm, "end": v(95.8, 16.17) * mm});
            skLineSegment(sketch, "E400.MirrorCS", {"start": v(4.76, 16.82) * mm, "end": v(50.05, 16.5) * mm});
            skLineSegment(sketch, "E401.MirrorCS", {"start": v(354.85, 14.3) * mm, "end": v(380.5, 14.12) * mm});
            skLineSegment(sketch, "E402.MirrorCS", {"start": v(257.7, 15) * mm, "end": v(288.8, 14.78) * mm});
            skLineSegment(sketch, "E403.MirrorCS", {"start": v(483.65, 13.38) * mm, "end": v(502.07, 13.24) * mm});
            skLineSegment(sketch, "E404.MirrorCS", {"start": v(410.87, 13.9) * mm, "end": v(433.37, 13.74) * mm});
            skLineSegment(sketch, "E405.MirrorCS", {"start": v(182.9, 15.54) * mm, "end": v(218.2, 15.29) * mm});
            skLineSegment(sketch, "E406.MirrorCS", {"start": v(460.78, 13.54) * mm, "end": v(480.48, 13.4) * mm});
            skLineSegment(sketch, "E407.MirrorCS", {"start": v(324.31, 14.52) * mm, "end": v(351.67, 14.33) * mm});
            skLineSegment(sketch, "E408.MirrorCS", {"start": v(98.97, 16.15) * mm, "end": v(138.98, 15.86) * mm});
            skLineSegment(sketch, "E409", {"start": v(0, 24.67) * mm, "end": v(648.25, 23.11) * mm, "construction": true});
            skLineSegment(sketch, "E410", {"start": v(0, 25.43) * mm, "end": v(642.98, 23.89) * mm, "construction": true});
            skLineSegment(sketch, "E411", {"start": v(4.76, 24.66) * mm, "end": v(4.76, 25.42) * mm});
            skLineSegment(sketch, "E412", {"start": v(4.76, 25.42) * mm, "end": v(50.06, 25.31) * mm});
            skLineSegment(sketch, "E413", {"start": v(50.06, 25.31) * mm, "end": v(50.06, 24.55) * mm});
            skLineSegment(sketch, "E414", {"start": v(53.23, 24.54) * mm, "end": v(53.23, 25.3) * mm});
            skLineSegment(sketch, "E415", {"start": v(53.23, 25.3) * mm, "end": v(95.8, 25.2) * mm});
            skLineSegment(sketch, "E416", {"start": v(95.8, 25.2) * mm, "end": v(95.8, 24.44) * mm});
            skLineSegment(sketch, "E417", {"start": v(98.98, 24.43) * mm, "end": v(98.98, 25.2) * mm});
            skLineSegment(sketch, "E418", {"start": v(98.98, 25.2) * mm, "end": v(139, 25.1) * mm});
            skLineSegment(sketch, "E419", {"start": v(139, 25.1) * mm, "end": v(138.99, 24.34) * mm});
            skLineSegment(sketch, "E420", {"start": v(142.16, 24.33) * mm, "end": v(142.17, 25.1) * mm});
            skLineSegment(sketch, "E421", {"start": v(142.17, 25.1) * mm, "end": v(179.74, 25) * mm});
            skLineSegment(sketch, "E422", {"start": v(179.74, 25) * mm, "end": v(179.74, 24.24) * mm});
            skLineSegment(sketch, "E423", {"start": v(182.91, 24.23) * mm, "end": v(182.92, 25) * mm});
            skLineSegment(sketch, "E424", {"start": v(182.92, 25) * mm, "end": v(218.22, 24.9) * mm, "construction": true});
            skLineSegment(sketch, "E425", {"start": v(218.22, 24.9) * mm, "end": v(218.22, 24.15) * mm});
            skLineSegment(sketch, "E426", {"start": v(221.4, 24.14) * mm, "end": v(221.4, 24.9) * mm});
            skLineSegment(sketch, "E427", {"start": v(221.4, 24.9) * mm, "end": v(254.53, 24.82) * mm});
            skLineSegment(sketch, "E428", {"start": v(254.53, 24.82) * mm, "end": v(254.53, 24.06) * mm});
            skLineSegment(sketch, "E429", {"start": v(257.7, 24.05) * mm, "end": v(257.7, 24.81) * mm});
            skLineSegment(sketch, "E430", {"start": v(257.7, 24.81) * mm, "end": v(288.8, 24.74) * mm});
            skLineSegment(sketch, "E431", {"start": v(288.8, 24.74) * mm, "end": v(288.8, 23.98) * mm});
            skLineSegment(sketch, "E432", {"start": v(291.98, 23.97) * mm, "end": v(291.98, 24.73) * mm});
            skLineSegment(sketch, "E433", {"start": v(291.98, 24.73) * mm, "end": v(321.15, 24.66) * mm});
            skLineSegment(sketch, "E434", {"start": v(321.15, 24.66) * mm, "end": v(321.15, 23.9) * mm});
            skLineSegment(sketch, "E435", {"start": v(324.33, 23.9) * mm, "end": v(324.33, 24.65) * mm});
            skLineSegment(sketch, "E436", {"start": v(324.33, 24.65) * mm, "end": v(351.69, 24.59) * mm});
            skLineSegment(sketch, "E437", {"start": v(351.69, 24.59) * mm, "end": v(351.69, 23.83) * mm});
            skLineSegment(sketch, "E438", {"start": v(182.92, 25) * mm, "end": v(218.22, 24.9) * mm});
            skLineSegment(sketch, "E439", {"start": v(354.86, 23.82) * mm, "end": v(354.86, 24.58) * mm});
            skLineSegment(sketch, "E440", {"start": v(354.86, 24.58) * mm, "end": v(380.5, 24.52) * mm});
            skLineSegment(sketch, "E441", {"start": v(380.5, 24.52) * mm, "end": v(380.5, 23.76) * mm});
            skLineSegment(sketch, "E442", {"start": v(383.68, 23.75) * mm, "end": v(383.68, 24.51) * mm});
            skLineSegment(sketch, "E443", {"start": v(383.68, 24.51) * mm, "end": v(407.71, 24.45) * mm});
            skLineSegment(sketch, "E444", {"start": v(407.71, 24.45) * mm, "end": v(407.7, 23.7) * mm});
            skLineSegment(sketch, "E445", {"start": v(410.88, 23.68) * mm, "end": v(410.89, 24.45) * mm});
            skLineSegment(sketch, "E446", {"start": v(410.89, 24.45) * mm, "end": v(433.39, 24.4) * mm});
            skLineSegment(sketch, "E447", {"start": v(433.39, 24.4) * mm, "end": v(433.39, 23.63) * mm});
            skLineSegment(sketch, "E448", {"start": v(436.56, 23.62) * mm, "end": v(436.56, 24.38) * mm});
            skLineSegment(sketch, "E449", {"start": v(436.56, 24.38) * mm, "end": v(457.62, 24.33) * mm});
            skLineSegment(sketch, "E450", {"start": v(457.62, 24.33) * mm, "end": v(457.62, 23.57) * mm});
            skLineSegment(sketch, "E451", {"start": v(460.8, 23.56) * mm, "end": v(460.8, 24.33) * mm});
            skLineSegment(sketch, "E452", {"start": v(460.8, 24.33) * mm, "end": v(480.5, 24.28) * mm});
            skLineSegment(sketch, "E453", {"start": v(480.5, 24.28) * mm, "end": v(480.5, 23.52) * mm});
            skLineSegment(sketch, "E454", {"start": v(483.67, 23.5) * mm, "end": v(483.67, 24.27) * mm});
            skLineSegment(sketch, "E455", {"start": v(483.67, 24.27) * mm, "end": v(502.09, 24.23) * mm});
            skLineSegment(sketch, "E456", {"start": v(502.09, 24.23) * mm, "end": v(502.09, 23.46) * mm});
            skLineSegment(sketch, "E457", {"start": v(505.26, 23.46) * mm, "end": v(505.26, 24.22) * mm});
            skLineSegment(sketch, "E458", {"start": v(505.26, 24.22) * mm, "end": v(522.47, 24.18) * mm});
            skLineSegment(sketch, "E459", {"start": v(522.47, 24.18) * mm, "end": v(522.47, 23.42) * mm});
            skLineSegment(sketch, "E460", {"start": v(525.64, 23.4) * mm, "end": v(525.64, 24.17) * mm});
            skLineSegment(sketch, "E461", {"start": v(525.64, 24.17) * mm, "end": v(541.7, 24.13) * mm});
            skLineSegment(sketch, "E462", {"start": v(541.7, 24.13) * mm, "end": v(541.7, 23.37) * mm});
            skLineSegment(sketch, "E463", {"start": v(544.88, 23.36) * mm, "end": v(544.88, 24.12) * mm});
            skLineSegment(sketch, "E464", {"start": v(544.88, 24.12) * mm, "end": v(559.86, 24.09) * mm});
            skLineSegment(sketch, "E465", {"start": v(559.86, 24.09) * mm, "end": v(559.86, 23.33) * mm});
            skLineSegment(sketch, "E466", {"start": v(563.03, 23.32) * mm, "end": v(563.03, 24.08) * mm});
            skLineSegment(sketch, "E467", {"start": v(563.03, 24.08) * mm, "end": v(577, 24.05) * mm});
            skLineSegment(sketch, "E468", {"start": v(577, 24.05) * mm, "end": v(577, 23.29) * mm});
            skLineSegment(sketch, "E469", {"start": v(580.17, 23.28) * mm, "end": v(580.17, 24.04) * mm});
            skLineSegment(sketch, "E470", {"start": v(580.17, 24.04) * mm, "end": v(593.17, 24) * mm});
            skLineSegment(sketch, "E471", {"start": v(593.17, 24) * mm, "end": v(593.17, 23.25) * mm});
            skLineSegment(sketch, "E472", {"start": v(596.34, 23.24) * mm, "end": v(596.35, 24) * mm});
            skLineSegment(sketch, "E473", {"start": v(596.35, 24) * mm, "end": v(608.44, 23.97) * mm});
            skLineSegment(sketch, "E474", {"start": v(608.44, 23.97) * mm, "end": v(608.44, 23.2) * mm});
            skLineSegment(sketch, "E475", {"start": v(611.61, 23.2) * mm, "end": v(611.61, 23.96) * mm});
            skLineSegment(sketch, "E476", {"start": v(611.61, 23.96) * mm, "end": v(622.85, 23.94) * mm});
            skLineSegment(sketch, "E477", {"start": v(622.85, 23.94) * mm, "end": v(622.85, 23.17) * mm});
            skLineSegment(sketch, "E478.MirrorCS", {"start": v(182.91, 24.23) * mm, "end": v(182.91, 23.47) * mm});
            skLineSegment(sketch, "E479.MirrorCS", {"start": v(608.43, 22.45) * mm, "end": v(608.44, 23.2) * mm});
            skLineSegment(sketch, "E480.MirrorCS", {"start": v(221.4, 24.14) * mm, "end": v(221.4, 23.38) * mm});
            skLineSegment(sketch, "E481.MirrorCS", {"start": v(559.86, 22.56) * mm, "end": v(559.86, 23.33) * mm});
            skLineSegment(sketch, "E482.MirrorCS", {"start": v(218.22, 23.38) * mm, "end": v(218.22, 24.15) * mm});
            skLineSegment(sketch, "E483.MirrorCS", {"start": v(291.98, 23.97) * mm, "end": v(291.98, 23.2) * mm});
            skLineSegment(sketch, "E484.MirrorCS", {"start": v(95.8, 23.68) * mm, "end": v(95.8, 24.44) * mm});
            skLineSegment(sketch, "E485.MirrorCS", {"start": v(50.06, 23.79) * mm, "end": v(50.06, 24.55) * mm});
            skLineSegment(sketch, "E486.MirrorCS", {"start": v(611.61, 23.2) * mm, "end": v(611.6, 22.44) * mm});
            skLineSegment(sketch, "E487.MirrorCS", {"start": v(596.34, 23.24) * mm, "end": v(596.34, 22.48) * mm});
            skLineSegment(sketch, "E488.MirrorCS", {"start": v(324.33, 23.9) * mm, "end": v(324.33, 23.13) * mm});
            skLineSegment(sketch, "E489.MirrorCS", {"start": v(580.17, 23.28) * mm, "end": v(580.17, 22.52) * mm});
            skLineSegment(sketch, "E490.MirrorCS", {"start": v(480.5, 22.75) * mm, "end": v(480.5, 23.52) * mm});
            skLineSegment(sketch, "E491.MirrorCS", {"start": v(407.7, 22.93) * mm, "end": v(407.7, 23.7) * mm});
            skLineSegment(sketch, "E492.MirrorCS", {"start": v(593.17, 22.48) * mm, "end": v(593.17, 23.25) * mm});
            skLineSegment(sketch, "E493.MirrorCS", {"start": v(483.67, 23.5) * mm, "end": v(483.67, 22.75) * mm});
            skLineSegment(sketch, "E494.MirrorCS", {"start": v(580.17, 22.52) * mm, "end": v(593.17, 22.48) * mm});
            skLineSegment(sketch, "E495.MirrorCS", {"start": v(522.46, 22.65) * mm, "end": v(522.47, 23.42) * mm});
            skLineSegment(sketch, "E496.MirrorCS", {"start": v(321.15, 23.14) * mm, "end": v(321.15, 23.9) * mm});
            skLineSegment(sketch, "E497.MirrorCS", {"start": v(457.62, 22.8) * mm, "end": v(457.62, 23.57) * mm});
            skLineSegment(sketch, "E498.MirrorCS", {"start": v(563.03, 23.32) * mm, "end": v(563.03, 22.56) * mm});
            skLineSegment(sketch, "E499.MirrorCS", {"start": v(383.68, 23.75) * mm, "end": v(383.68, 22.99) * mm});
            skLineSegment(sketch, "E500.MirrorCS", {"start": v(380.5, 23) * mm, "end": v(380.5, 23.76) * mm});
            skLineSegment(sketch, "E501.MirrorCS", {"start": v(505.26, 23.46) * mm, "end": v(505.26, 22.7) * mm});
            skLineSegment(sketch, "E502.MirrorCS", {"start": v(596.34, 22.48) * mm, "end": v(608.43, 22.45) * mm});
            skLineSegment(sketch, "E503.MirrorCS", {"start": v(544.87, 22.6) * mm, "end": v(559.86, 22.56) * mm});
            skLineSegment(sketch, "E504.MirrorCS", {"start": v(142.16, 24.33) * mm, "end": v(142.16, 23.57) * mm});
            skLineSegment(sketch, "E505.MirrorCS", {"start": v(138.99, 23.57) * mm, "end": v(138.99, 24.34) * mm});
            skLineSegment(sketch, "E506.MirrorCS", {"start": v(98.98, 24.43) * mm, "end": v(98.98, 23.67) * mm});
            skLineSegment(sketch, "E507.MirrorCS", {"start": v(53.23, 24.54) * mm, "end": v(53.23, 23.78) * mm});
            skLineSegment(sketch, "E508.MirrorCS", {"start": v(4.76, 24.66) * mm, "end": v(4.76, 23.9) * mm});
            skLineSegment(sketch, "E509.MirrorCS", {"start": v(179.74, 23.48) * mm, "end": v(179.74, 24.24) * mm});
            skLineSegment(sketch, "E510.MirrorCS", {"start": v(433.38, 22.87) * mm, "end": v(433.39, 23.63) * mm});
            skLineSegment(sketch, "E511.MirrorCS", {"start": v(544.88, 23.36) * mm, "end": v(544.87, 22.6) * mm});
            skLineSegment(sketch, "E512.MirrorCS", {"start": v(502.09, 22.7) * mm, "end": v(502.09, 23.46) * mm});
            skLineSegment(sketch, "E513.MirrorCS", {"start": v(288.8, 23.21) * mm, "end": v(288.8, 23.98) * mm});
            skLineSegment(sketch, "E514.MirrorCS", {"start": v(563.03, 22.56) * mm, "end": v(577, 22.52) * mm});
            skLineSegment(sketch, "E515.MirrorCS", {"start": v(254.53, 23.3) * mm, "end": v(254.53, 24.06) * mm});
            skLineSegment(sketch, "E516.MirrorCS", {"start": v(611.6, 22.44) * mm, "end": v(622.84, 22.41) * mm});
            skLineSegment(sketch, "E517.MirrorCS", {"start": v(525.64, 23.4) * mm, "end": v(525.64, 22.65) * mm});
            skLineSegment(sketch, "E518.MirrorCS", {"start": v(351.68, 23.06) * mm, "end": v(351.69, 23.83) * mm});
            skLineSegment(sketch, "E519.MirrorCS", {"start": v(410.88, 23.68) * mm, "end": v(410.88, 22.92) * mm});
            skLineSegment(sketch, "E520.MirrorCS", {"start": v(577, 22.52) * mm, "end": v(577, 23.29) * mm});
            skLineSegment(sketch, "E521.MirrorCS", {"start": v(257.7, 24.05) * mm, "end": v(257.7, 23.29) * mm});
            skLineSegment(sketch, "E522.MirrorCS", {"start": v(622.84, 22.41) * mm, "end": v(622.85, 23.17) * mm});
            skLineSegment(sketch, "E523.MirrorCS", {"start": v(354.86, 23.82) * mm, "end": v(354.86, 23.06) * mm});
            skLineSegment(sketch, "E524.MirrorCS", {"start": v(505.26, 22.7) * mm, "end": v(522.46, 22.65) * mm});
            skLineSegment(sketch, "E525.MirrorCS", {"start": v(436.56, 23.62) * mm, "end": v(436.56, 22.86) * mm});
            skLineSegment(sketch, "E526.MirrorCS", {"start": v(182.91, 23.47) * mm, "end": v(218.22, 23.38) * mm, "construction": true});
            skLineSegment(sketch, "E527.MirrorCS", {"start": v(460.8, 23.56) * mm, "end": v(460.8, 22.8) * mm});
            skLineSegment(sketch, "E528.MirrorCS", {"start": v(541.7, 22.6) * mm, "end": v(541.7, 23.37) * mm});
            skLineSegment(sketch, "E529.MirrorCS", {"start": v(525.64, 22.65) * mm, "end": v(541.7, 22.6) * mm});
            skLineSegment(sketch, "E530.MirrorCS", {"start": v(221.4, 23.38) * mm, "end": v(254.53, 23.3) * mm});
            skLineSegment(sketch, "E531.MirrorCS", {"start": v(383.68, 22.99) * mm, "end": v(407.7, 22.93) * mm});
            skLineSegment(sketch, "E532.MirrorCS", {"start": v(291.98, 23.2) * mm, "end": v(321.15, 23.14) * mm});
            skLineSegment(sketch, "E533.MirrorCS", {"start": v(436.56, 22.86) * mm, "end": v(457.62, 22.8) * mm});
            skLineSegment(sketch, "E534.MirrorCS", {"start": v(142.16, 23.57) * mm, "end": v(179.74, 23.48) * mm});
            skLineSegment(sketch, "E535.MirrorCS", {"start": v(53.23, 23.78) * mm, "end": v(95.8, 23.68) * mm});
            skLineSegment(sketch, "E536.MirrorCS", {"start": v(4.76, 23.9) * mm, "end": v(50.06, 23.79) * mm});
            skLineSegment(sketch, "E537.MirrorCS", {"start": v(354.86, 23.06) * mm, "end": v(380.5, 23) * mm});
            skLineSegment(sketch, "E538.MirrorCS", {"start": v(257.7, 23.29) * mm, "end": v(288.8, 23.21) * mm});
            skLineSegment(sketch, "E539.MirrorCS", {"start": v(483.67, 22.75) * mm, "end": v(502.09, 22.7) * mm});
            skLineSegment(sketch, "E540.MirrorCS", {"start": v(410.88, 22.92) * mm, "end": v(433.38, 22.87) * mm});
            skLineSegment(sketch, "E541.MirrorCS", {"start": v(182.91, 23.47) * mm, "end": v(218.22, 23.38) * mm});
            skLineSegment(sketch, "E542.MirrorCS", {"start": v(460.8, 22.8) * mm, "end": v(480.5, 22.75) * mm});
            skLineSegment(sketch, "E543.MirrorCS", {"start": v(324.33, 23.13) * mm, "end": v(351.68, 23.06) * mm});
            skLineSegment(sketch, "E544.MirrorCS", {"start": v(98.98, 23.67) * mm, "end": v(138.99, 23.57) * mm});
            skLineSegment(sketch, "E545", {"start": v(0, 28.2) * mm, "end": v(665.02, 28.2) * mm, "construction": true});
            skLineSegment(sketch, "E546.MirrorCS", {"start": v(218.2, 41.1) * mm, "end": v(218.21, 40.34) * mm});
            skLineSegment(sketch, "E547.MirrorCS", {"start": v(218.22, 39.58) * mm, "end": v(218.21, 40.34) * mm});
            skLineSegment(sketch, "E548.MirrorCS", {"start": v(182.91, 40.08) * mm, "end": v(182.92, 39.32) * mm});
            skLineSegment(sketch, "E549.MirrorCS", {"start": v(95.78, 55.24) * mm, "end": v(95.8, 54.47) * mm});
            skLineSegment(sketch, "E550.MirrorCS", {"start": v(50.04, 54.47) * mm, "end": v(50.05, 53.7) * mm});
            skLineSegment(sketch, "E551.MirrorCS", {"start": v(182.91, 40.08) * mm, "end": v(182.9, 40.85) * mm});
            skLineSegment(sketch, "E552.MirrorCS", {"start": v(218.21, 47.67) * mm, "end": v(218.2, 48.43) * mm});
            skLineSegment(sketch, "E553.MirrorCS", {"start": v(351.67, 49.27) * mm, "end": v(351.66, 50.04) * mm});
            skLineSegment(sketch, "E554.MirrorCS", {"start": v(354.84, 50.07) * mm, "end": v(354.85, 49.31) * mm});
            skLineSegment(sketch, "E555.MirrorCS", {"start": v(4.76, 38.8) * mm, "end": v(4.77, 38.04) * mm});
            skLineSegment(sketch, "E556.MirrorCS", {"start": v(324.3, 49.7) * mm, "end": v(324.31, 48.95) * mm});
            skLineSegment(sketch, "E557.MirrorCS", {"start": v(218.2, 49.2) * mm, "end": v(218.2, 48.43) * mm});
            skLineSegment(sketch, "E558.MirrorCS", {"start": v(53.23, 53.76) * mm, "end": v(53.21, 54.52) * mm});
            skLineSegment(sketch, "E559.MirrorCS", {"start": v(98.97, 54.53) * mm, "end": v(98.96, 55.29) * mm});
            skLineSegment(sketch, "E560.MirrorCS", {"start": v(324.32, 41.1) * mm, "end": v(324.31, 41.86) * mm});
            skLineSegment(sketch, "E561.MirrorCS", {"start": v(321.12, 50.43) * mm, "end": v(321.13, 49.67) * mm});
            skLineSegment(sketch, "E562.MirrorCS", {"start": v(541.65, 53.08) * mm, "end": v(541.66, 52.32) * mm});
            skLineSegment(sketch, "E563.MirrorCS", {"start": v(291.96, 49.32) * mm, "end": v(291.97, 48.56) * mm});
            skLineSegment(sketch, "E564.MirrorCS", {"start": v(95.8, 46.2) * mm, "end": v(95.8, 46.96) * mm});
            skLineSegment(sketch, "E565.MirrorCS", {"start": v(410.88, 41.73) * mm, "end": v(410.87, 42.49) * mm});
            skLineSegment(sketch, "E566.MirrorCS", {"start": v(522.42, 52.85) * mm, "end": v(522.43, 52.08) * mm});
            skLineSegment(sketch, "E567.MirrorCS", {"start": v(288.8, 48.52) * mm, "end": v(288.78, 49.28) * mm});
            skLineSegment(sketch, "E568.MirrorCS", {"start": v(544.84, 52.35) * mm, "end": v(544.85, 51.6) * mm});
            skLineSegment(sketch, "E569.MirrorCS", {"start": v(608.38, 53.88) * mm, "end": v(608.4, 53.12) * mm});
            skLineSegment(sketch, "E570.MirrorCS", {"start": v(611.6, 43.17) * mm, "end": v(611.6, 43.93) * mm});
            skLineSegment(sketch, "E571.MirrorCS", {"start": v(541.67, 51.55) * mm, "end": v(541.66, 52.32) * mm});
            skLineSegment(sketch, "E572.MirrorCS", {"start": v(182.9, 48.01) * mm, "end": v(182.9, 48.77) * mm});
            skLineSegment(sketch, "E573.MirrorCS", {"start": v(53.23, 46.45) * mm, "end": v(53.24, 45.7) * mm});
            skLineSegment(sketch, "E574.MirrorCS", {"start": v(182.91, 32.16) * mm, "end": v(182.91, 32.92) * mm});
            skLineSegment(sketch, "E575.MirrorCS", {"start": v(480.5, 41.46) * mm, "end": v(480.49, 42.23) * mm});
            skLineSegment(sketch, "E576.MirrorCS", {"start": v(179.72, 48.73) * mm, "end": v(179.73, 47.97) * mm});
            skLineSegment(sketch, "E577.MirrorCS", {"start": v(257.69, 48.9) * mm, "end": v(257.7, 48.15) * mm});
            skLineSegment(sketch, "E578.MirrorCS", {"start": v(50.06, 45.65) * mm, "end": v(50.05, 46.42) * mm});
            skLineSegment(sketch, "E579.MirrorCS", {"start": v(179.74, 32.91) * mm, "end": v(179.74, 32.15) * mm});
            skLineSegment(sketch, "E580.MirrorCS", {"start": v(50.05, 39.89) * mm, "end": v(50.06, 39.13) * mm});
            skLineSegment(sketch, "E581.MirrorCS", {"start": v(480.45, 52.34) * mm, "end": v(480.46, 51.58) * mm});
            skLineSegment(sketch, "E582.MirrorCS", {"start": v(608.4, 52.35) * mm, "end": v(608.4, 53.12) * mm});
            skLineSegment(sketch, "E583.MirrorCS", {"start": v(522.44, 51.32) * mm, "end": v(522.43, 52.08) * mm});
            skLineSegment(sketch, "E584.MirrorCS", {"start": v(4.76, 45.87) * mm, "end": v(4.77, 45.11) * mm});
            skLineSegment(sketch, "E585.MirrorCS", {"start": v(354.84, 50.07) * mm, "end": v(354.83, 50.84) * mm});
            skLineSegment(sketch, "E586.MirrorCS", {"start": v(53.23, 46.45) * mm, "end": v(53.22, 47.22) * mm});
            skLineSegment(sketch, "E587.MirrorCS", {"start": v(324.32, 41.1) * mm, "end": v(324.33, 40.34) * mm});
            skLineSegment(sketch, "E588.MirrorCS", {"start": v(139, 39) * mm, "end": v(138.99, 39.77) * mm});
            skLineSegment(sketch, "E589.MirrorCS", {"start": v(291.97, 40.87) * mm, "end": v(291.97, 41.63) * mm});
            skLineSegment(sketch, "E590.MirrorCS", {"start": v(4.76, 45.87) * mm, "end": v(4.75, 46.63) * mm});
            skLineSegment(sketch, "E591.MirrorCS", {"start": v(4.76, 52.94) * mm, "end": v(4.77, 52.18) * mm});
            skLineSegment(sketch, "E592.MirrorCS", {"start": v(50.06, 52.94) * mm, "end": v(50.05, 53.7) * mm});
            skLineSegment(sketch, "E593.MirrorCS", {"start": v(53.23, 53.76) * mm, "end": v(53.24, 53) * mm});
            skLineSegment(sketch, "E594.MirrorCS", {"start": v(95.8, 53.71) * mm, "end": v(95.8, 54.47) * mm});
            skLineSegment(sketch, "E595.MirrorCS", {"start": v(98.97, 54.53) * mm, "end": v(98.98, 53.76) * mm});
            skLineSegment(sketch, "E596.MirrorCS", {"start": v(351.65, 50.8) * mm, "end": v(351.66, 50.04) * mm});
            skLineSegment(sketch, "E597.MirrorCS", {"start": v(98.98, 39.48) * mm, "end": v(98.99, 38.72) * mm});
            skLineSegment(sketch, "E598.MirrorCS", {"start": v(179.74, 31.39) * mm, "end": v(179.74, 32.15) * mm});
            skLineSegment(sketch, "E599.MirrorCS", {"start": v(257.69, 48.9) * mm, "end": v(257.68, 49.67) * mm});
            skLineSegment(sketch, "E600.MirrorCS", {"start": v(380.5, 49.62) * mm, "end": v(380.48, 50.38) * mm});
            skLineSegment(sketch, "E601.MirrorCS", {"start": v(257.7, 40.62) * mm, "end": v(257.7, 39.86) * mm});
            skLineSegment(sketch, "E602.MirrorCS", {"start": v(410.88, 41.73) * mm, "end": v(410.88, 40.96) * mm});
            skLineSegment(sketch, "E603.MirrorCS", {"start": v(50.06, 38.37) * mm, "end": v(50.06, 39.13) * mm});
            skLineSegment(sketch, "E604.MirrorCS", {"start": v(480.47, 50.82) * mm, "end": v(480.46, 51.58) * mm});
            skLineSegment(sketch, "E605.MirrorCS", {"start": v(50.05, 47.18) * mm, "end": v(50.05, 46.42) * mm});
            skLineSegment(sketch, "E606.MirrorCS", {"start": v(221.39, 40.36) * mm, "end": v(221.38, 41.12) * mm});
            skLineSegment(sketch, "E607.MirrorCS", {"start": v(291.97, 40.87) * mm, "end": v(291.98, 40.1) * mm});
            skLineSegment(sketch, "E608.MirrorCS", {"start": v(324.3, 49.7) * mm, "end": v(324.3, 50.47) * mm});
            skLineSegment(sketch, "E609.MirrorCS", {"start": v(608.42, 43.9) * mm, "end": v(608.42, 43.15) * mm});
            skLineSegment(sketch, "E610.MirrorCS", {"start": v(182.9, 48.01) * mm, "end": v(182.91, 47.25) * mm});
            skLineSegment(sketch, "E611.MirrorCS", {"start": v(380.47, 51.14) * mm, "end": v(380.48, 50.38) * mm});
            skLineSegment(sketch, "E612.MirrorCS", {"start": v(95.8, 47.73) * mm, "end": v(95.8, 46.96) * mm});
            skLineSegment(sketch, "E613.MirrorCS", {"start": v(4.76, 38.8) * mm, "end": v(4.76, 39.56) * mm});
            skLineSegment(sketch, "E614.MirrorCS", {"start": v(4.76, 52.94) * mm, "end": v(4.75, 53.7) * mm});
            skLineSegment(sketch, "E615.MirrorCS", {"start": v(291.96, 49.32) * mm, "end": v(291.95, 50.08) * mm});
            skLineSegment(sketch, "E616.MirrorCS", {"start": v(53.23, 39.15) * mm, "end": v(53.23, 39.91) * mm});
            skLineSegment(sketch, "E617.MirrorCS", {"start": v(611.6, 43.17) * mm, "end": v(611.6, 42.4) * mm});
            skLineSegment(sketch, "E618.MirrorCS", {"start": v(288.77, 50.04) * mm, "end": v(288.78, 49.28) * mm});
            skLineSegment(sketch, "E619.MirrorCS", {"start": v(321.14, 48.9) * mm, "end": v(321.13, 49.67) * mm});
            skLineSegment(sketch, "E620.MirrorCS", {"start": v(480.48, 42.99) * mm, "end": v(480.49, 42.23) * mm});
            skLineSegment(sketch, "E621.MirrorCS", {"start": v(98.98, 39.48) * mm, "end": v(98.97, 40.24) * mm});
            skLineSegment(sketch, "E622.MirrorCS", {"start": v(221.39, 40.36) * mm, "end": v(221.4, 39.6) * mm});
            skLineSegment(sketch, "E623.MirrorCS", {"start": v(608.43, 42.39) * mm, "end": v(608.42, 43.15) * mm});
            skLineSegment(sketch, "E624.MirrorCS", {"start": v(257.7, 40.62) * mm, "end": v(257.7, 41.38) * mm});
            skLineSegment(sketch, "E625.MirrorCS", {"start": v(138.98, 40.53) * mm, "end": v(138.99, 39.77) * mm});
            skLineSegment(sketch, "E626.MirrorCS", {"start": v(580.09, 62.61) * mm, "end": v(580.08, 63.37) * mm});
            skLineSegment(sketch, "E627.MirrorCS", {"start": v(218.2, 55.77) * mm, "end": v(218.19, 56.53) * mm});
            skLineSegment(sketch, "E628.MirrorCS", {"start": v(95.8, 31.19) * mm, "end": v(95.8, 31.95) * mm});
            skLineSegment(sketch, "E629.MirrorCS", {"start": v(142.16, 39.8) * mm, "end": v(142.16, 40.55) * mm});
            skLineSegment(sketch, "E630.MirrorCS", {"start": v(576.98, 43.68) * mm, "end": v(576.98, 42.92) * mm});
            skLineSegment(sketch, "E631.MirrorCS", {"start": v(502.04, 52.6) * mm, "end": v(502.05, 51.84) * mm});
            skLineSegment(sketch, "E632.MirrorCS", {"start": v(436.53, 51.05) * mm, "end": v(436.54, 50.3) * mm});
            skLineSegment(sketch, "E633.MirrorCS", {"start": v(544.84, 52.35) * mm, "end": v(544.83, 53.12) * mm});
            skLineSegment(sketch, "E634.MirrorCS", {"start": v(460.76, 51.34) * mm, "end": v(460.76, 52.1) * mm});
            skLineSegment(sketch, "E635.MirrorCS", {"start": v(433.37, 50.25) * mm, "end": v(433.36, 51.02) * mm});
            skLineSegment(sketch, "E636.MirrorCS", {"start": v(576.9, 63.32) * mm, "end": v(576.91, 62.56) * mm});
            skLineSegment(sketch, "E637.MirrorCS", {"start": v(179.74, 39.3) * mm, "end": v(179.74, 40.06) * mm});
            skLineSegment(sketch, "E638.MirrorCS", {"start": v(433.35, 51.78) * mm, "end": v(433.36, 51.02) * mm});
            skLineSegment(sketch, "E639.MirrorCS", {"start": v(53.23, 31.85) * mm, "end": v(53.23, 31.08) * mm});
            skLineSegment(sketch, "E640.MirrorCS", {"start": v(483.64, 51.62) * mm, "end": v(483.63, 52.38) * mm});
            skLineSegment(sketch, "E641.MirrorCS", {"start": v(436.53, 51.05) * mm, "end": v(436.52, 51.82) * mm});
            skLineSegment(sketch, "E642.MirrorCS", {"start": v(410.86, 50.75) * mm, "end": v(410.87, 49.98) * mm});
            skLineSegment(sketch, "E643.MirrorCS", {"start": v(50.06, 31.08) * mm, "end": v(50.06, 31.84) * mm});
            skLineSegment(sketch, "E644.MirrorCS", {"start": v(457.6, 42.82) * mm, "end": v(457.61, 42.06) * mm});
            skLineSegment(sketch, "E645.MirrorCS", {"start": v(138.99, 32.81) * mm, "end": v(138.99, 32.05) * mm});
            skLineSegment(sketch, "E646.MirrorCS", {"start": v(383.63, 59.3) * mm, "end": v(383.62, 60.07) * mm});
            skLineSegment(sketch, "E647.MirrorCS", {"start": v(291.94, 57.77) * mm, "end": v(291.92, 58.53) * mm});
            skLineSegment(sketch, "E648.MirrorCS", {"start": v(383.66, 50.42) * mm, "end": v(383.66, 49.66) * mm});
            skLineSegment(sketch, "E649.MirrorCS", {"start": v(98.97, 47) * mm, "end": v(98.97, 47.76) * mm});
            skLineSegment(sketch, "E650.MirrorCS", {"start": v(457.62, 41.3) * mm, "end": v(457.61, 42.06) * mm});
            skLineSegment(sketch, "E651.MirrorCS", {"start": v(563.02, 42.82) * mm, "end": v(563.01, 43.58) * mm});
            skLineSegment(sketch, "E652.MirrorCS", {"start": v(98.98, 31.96) * mm, "end": v(98.98, 32.72) * mm});
            skLineSegment(sketch, "E653.MirrorCS", {"start": v(611.57, 53.15) * mm, "end": v(611.58, 52.4) * mm});
            skLineSegment(sketch, "E654.MirrorCS", {"start": v(254.52, 41.36) * mm, "end": v(254.52, 40.6) * mm});
            skLineSegment(sketch, "E655.MirrorCS", {"start": v(4.76, 31.73) * mm, "end": v(4.76, 30.97) * mm});
            skLineSegment(sketch, "E656.MirrorCS", {"start": v(53.23, 31.85) * mm, "end": v(53.23, 32.6) * mm});
            skLineSegment(sketch, "E657.MirrorCS", {"start": v(525.6, 52.12) * mm, "end": v(525.61, 51.36) * mm});
            skLineSegment(sketch, "E658.MirrorCS", {"start": v(142.16, 39.8) * mm, "end": v(142.17, 39.03) * mm});
            skLineSegment(sketch, "E659.MirrorCS", {"start": v(611.6, 43.93) * mm, "end": v(622.83, 44.01) * mm});
            skLineSegment(sketch, "E660.MirrorCS", {"start": v(95.8, 40.22) * mm, "end": v(95.8, 39.46) * mm});
            skLineSegment(sketch, "E661.MirrorCS", {"start": v(4.76, 31.73) * mm, "end": v(4.76, 32.5) * mm});
            skLineSegment(sketch, "E662.MirrorCS", {"start": v(182.89, 55.94) * mm, "end": v(182.9, 55.17) * mm});
            skLineSegment(sketch, "E663.MirrorCS", {"start": v(53.23, 39.15) * mm, "end": v(53.24, 38.39) * mm});
            skLineSegment(sketch, "E664.MirrorCS", {"start": v(483.64, 51.62) * mm, "end": v(483.65, 50.86) * mm});
            skLineSegment(sketch, "E665.MirrorCS", {"start": v(611.57, 53.15) * mm, "end": v(611.56, 53.92) * mm});
            skLineSegment(sketch, "E666.MirrorCS", {"start": v(179.74, 47.21) * mm, "end": v(179.73, 47.97) * mm});
            skLineSegment(sketch, "E667.MirrorCS", {"start": v(608.34, 63.85) * mm, "end": v(608.35, 63.09) * mm});
            skLineSegment(sketch, "E668.MirrorCS", {"start": v(522.38, 62.4) * mm, "end": v(522.4, 61.64) * mm});
            skLineSegment(sketch, "E669.MirrorCS", {"start": v(525.63, 42.55) * mm, "end": v(525.62, 43.31) * mm});
            skLineSegment(sketch, "E670.MirrorCS", {"start": v(182.89, 55.94) * mm, "end": v(182.88, 56.7) * mm});
            skLineSegment(sketch, "E671.MirrorCS", {"start": v(218.18, 57.3) * mm, "end": v(218.19, 56.53) * mm});
            skLineSegment(sketch, "E672.MirrorCS", {"start": v(179.73, 40.82) * mm, "end": v(179.74, 40.06) * mm});
            skLineSegment(sketch, "E673.MirrorCS", {"start": v(436.55, 41.9) * mm, "end": v(436.55, 42.67) * mm});
            skLineSegment(sketch, "E674.MirrorCS", {"start": v(562.95, 62.32) * mm, "end": v(562.97, 61.56) * mm});
            skLineSegment(sketch, "E675.MirrorCS", {"start": v(622.84, 42.49) * mm, "end": v(622.83, 43.25) * mm});
            skLineSegment(sketch, "E676.MirrorCS", {"start": v(525.6, 52.12) * mm, "end": v(525.6, 52.88) * mm});
            skLineSegment(sketch, "E677.MirrorCS", {"start": v(580.13, 52.78) * mm, "end": v(580.14, 52.02) * mm});
            skLineSegment(sketch, "E678.MirrorCS", {"start": v(142.16, 32.06) * mm, "end": v(142.16, 32.82) * mm});
            skLineSegment(sketch, "E679.MirrorCS", {"start": v(95.81, 38.7) * mm, "end": v(95.8, 39.46) * mm});
            skLineSegment(sketch, "E680.MirrorCS", {"start": v(142.15, 47.52) * mm, "end": v(142.15, 48.28) * mm});
            skLineSegment(sketch, "E681.MirrorCS", {"start": v(576.94, 53.5) * mm, "end": v(576.95, 52.74) * mm});
            skLineSegment(sketch, "E682.MirrorCS", {"start": v(502.06, 51.08) * mm, "end": v(502.05, 51.84) * mm});
            skLineSegment(sketch, "E683.MirrorCS", {"start": v(182.91, 32.16) * mm, "end": v(182.92, 31.4) * mm});
            skLineSegment(sketch, "E684.MirrorCS", {"start": v(522.45, 43.3) * mm, "end": v(522.45, 42.53) * mm});
            skLineSegment(sketch, "E685.MirrorCS", {"start": v(410.86, 50.75) * mm, "end": v(410.85, 51.5) * mm});
            skLineSegment(sketch, "E686.MirrorCS", {"start": v(291.94, 57.77) * mm, "end": v(291.95, 57) * mm});
            skLineSegment(sketch, "E687.MirrorCS", {"start": v(436.5, 60.2) * mm, "end": v(436.51, 59.44) * mm});
            skLineSegment(sketch, "E688.MirrorCS", {"start": v(254.53, 39.84) * mm, "end": v(254.52, 40.6) * mm});
            skLineSegment(sketch, "E689.MirrorCS", {"start": v(407.7, 40.94) * mm, "end": v(407.7, 41.7) * mm});
            skLineSegment(sketch, "E690.MirrorCS", {"start": v(525.63, 42.55) * mm, "end": v(525.63, 41.79) * mm});
            skLineSegment(sketch, "E691.MirrorCS", {"start": v(611.6, 42.4) * mm, "end": v(622.84, 42.49) * mm});
            skLineSegment(sketch, "E692.MirrorCS", {"start": v(576.96, 51.98) * mm, "end": v(576.95, 52.74) * mm});
            skLineSegment(sketch, "E693.MirrorCS", {"start": v(436.5, 60.2) * mm, "end": v(436.49, 60.96) * mm});
            skLineSegment(sketch, "E694.MirrorCS", {"start": v(179.7, 56.65) * mm, "end": v(179.72, 55.88) * mm});
            skLineSegment(sketch, "E695.MirrorCS", {"start": v(142.15, 47.52) * mm, "end": v(142.16, 46.76) * mm});
            skLineSegment(sketch, "E696.MirrorCS", {"start": v(95.8, 32.71) * mm, "end": v(95.8, 31.95) * mm});
            skLineSegment(sketch, "E697.MirrorCS", {"start": v(142.16, 32.06) * mm, "end": v(142.17, 31.3) * mm});
            skLineSegment(sketch, "E698.MirrorCS", {"start": v(383.66, 50.42) * mm, "end": v(383.65, 51.18) * mm});
            skLineSegment(sketch, "E699.MirrorCS", {"start": v(460.76, 51.34) * mm, "end": v(460.77, 50.58) * mm});
            skLineSegment(sketch, "E700.MirrorCS", {"start": v(593.07, 63.6) * mm, "end": v(593.09, 62.83) * mm});
            skLineSegment(sketch, "E701.MirrorCS", {"start": v(139, 31.29) * mm, "end": v(138.99, 32.05) * mm});
            skLineSegment(sketch, "E702.MirrorCS", {"start": v(407.7, 42.46) * mm, "end": v(407.7, 41.7) * mm});
            skLineSegment(sketch, "E703.MirrorCS", {"start": v(522.46, 41.77) * mm, "end": v(522.45, 42.53) * mm});
            skLineSegment(sketch, "E704.MirrorCS", {"start": v(563, 52.57) * mm, "end": v(563, 51.8) * mm});
            skLineSegment(sketch, "E705.MirrorCS", {"start": v(522.4, 60.88) * mm, "end": v(522.4, 61.64) * mm});
            skLineSegment(sketch, "E706.MirrorCS", {"start": v(622.83, 44.01) * mm, "end": v(622.83, 43.25) * mm});
            skLineSegment(sketch, "E707.MirrorCS", {"start": v(98.97, 47) * mm, "end": v(98.98, 46.24) * mm});
            skLineSegment(sketch, "E708.MirrorCS", {"start": v(383.63, 59.3) * mm, "end": v(383.64, 58.55) * mm});
            skLineSegment(sketch, "E709.MirrorCS", {"start": v(608.36, 62.32) * mm, "end": v(608.35, 63.09) * mm});
            skLineSegment(sketch, "E710.MirrorCS", {"start": v(98.98, 31.96) * mm, "end": v(98.98, 31.2) * mm});
            skLineSegment(sketch, "E711.MirrorCS", {"start": v(559.83, 51.77) * mm, "end": v(559.82, 52.53) * mm});
            skLineSegment(sketch, "E712.MirrorCS", {"start": v(559.8, 53.3) * mm, "end": v(559.82, 52.53) * mm});
            skLineSegment(sketch, "E713.MirrorCS", {"start": v(380.47, 58.5) * mm, "end": v(380.45, 59.26) * mm});
            skLineSegment(sketch, "E714.MirrorCS", {"start": v(505.2, 61.35) * mm, "end": v(505.2, 60.6) * mm});
            skLineSegment(sketch, "E715.MirrorCS", {"start": v(596.27, 62.12) * mm, "end": v(608.36, 62.32) * mm});
            skLineSegment(sketch, "E716.MirrorCS", {"start": v(291.98, 32.42) * mm, "end": v(291.98, 31.66) * mm});
            skLineSegment(sketch, "E717.MirrorCS", {"start": v(502.08, 41.62) * mm, "end": v(502.08, 42.38) * mm});
            skLineSegment(sketch, "E718.MirrorCS", {"start": v(596.33, 43.06) * mm, "end": v(596.34, 42.3) * mm});
            skLineSegment(sketch, "E719.MirrorCS", {"start": v(221.38, 48.47) * mm, "end": v(221.37, 49.23) * mm});
            skLineSegment(sketch, "E720.MirrorCS", {"start": v(257.67, 57.2) * mm, "end": v(257.66, 57.95) * mm});
            skLineSegment(sketch, "E721.MirrorCS", {"start": v(596.33, 43.06) * mm, "end": v(596.32, 43.82) * mm});
            skLineSegment(sketch, "E722.MirrorCS", {"start": v(354.85, 41.32) * mm, "end": v(354.86, 40.56) * mm});
            skLineSegment(sketch, "E723.MirrorCS", {"start": v(142.14, 55.25) * mm, "end": v(142.13, 56.01) * mm});
            skLineSegment(sketch, "E724.MirrorCS", {"start": v(502.03, 60.54) * mm, "end": v(502.02, 61.3) * mm});
            skLineSegment(sketch, "E725.MirrorCS", {"start": v(596.26, 62.88) * mm, "end": v(596.27, 62.12) * mm});
            skLineSegment(sketch, "E726.MirrorCS", {"start": v(324.28, 58.31) * mm, "end": v(324.27, 59.07) * mm});
            skLineSegment(sketch, "E727.MirrorCS", {"start": v(596.32, 43.82) * mm, "end": v(608.42, 43.9) * mm});
            skLineSegment(sketch, "E728.MirrorCS", {"start": v(351.67, 42.06) * mm, "end": v(351.68, 41.3) * mm});
            skLineSegment(sketch, "E729.MirrorCS", {"start": v(483.66, 42.25) * mm, "end": v(483.67, 41.49) * mm});
            skLineSegment(sketch, "E730.MirrorCS", {"start": v(580.12, 53.54) * mm, "end": v(593.12, 53.7) * mm});
            skLineSegment(sketch, "E731.MirrorCS", {"start": v(593.1, 62.07) * mm, "end": v(593.09, 62.83) * mm});
            skLineSegment(sketch, "E732.MirrorCS", {"start": v(596.26, 62.88) * mm, "end": v(596.25, 63.64) * mm});
            skLineSegment(sketch, "E733.MirrorCS", {"start": v(351.68, 40.54) * mm, "end": v(351.68, 41.3) * mm});
            skLineSegment(sketch, "E734.MirrorCS", {"start": v(580.16, 42.94) * mm, "end": v(580.16, 42.18) * mm});
            skLineSegment(sketch, "E735.MirrorCS", {"start": v(622.81, 52.53) * mm, "end": v(622.8, 53.29) * mm});
            skLineSegment(sketch, "E736.MirrorCS", {"start": v(596.25, 63.64) * mm, "end": v(608.34, 63.85) * mm});
            skLineSegment(sketch, "E737.MirrorCS", {"start": v(483.6, 60.99) * mm, "end": v(483.62, 60.23) * mm});
            skLineSegment(sketch, "E738.MirrorCS", {"start": v(580.1, 61.85) * mm, "end": v(593.1, 62.07) * mm});
            skLineSegment(sketch, "E739.MirrorCS", {"start": v(611.53, 63.14) * mm, "end": v(611.51, 63.9) * mm});
            skLineSegment(sketch, "E740.MirrorCS", {"start": v(505.25, 42.4) * mm, "end": v(505.25, 43.17) * mm});
            skLineSegment(sketch, "E741.MirrorCS", {"start": v(288.8, 41.6) * mm, "end": v(288.8, 40.85) * mm});
            skLineSegment(sketch, "E742.MirrorCS", {"start": v(559.84, 43.56) * mm, "end": v(559.84, 42.8) * mm});
            skLineSegment(sketch, "E743.MirrorCS", {"start": v(559.85, 42.04) * mm, "end": v(559.84, 42.8) * mm});
            skLineSegment(sketch, "E744.MirrorCS", {"start": v(218.22, 31.48) * mm, "end": v(218.22, 32.24) * mm});
            skLineSegment(sketch, "E745.MirrorCS", {"start": v(562.97, 61.56) * mm, "end": v(576.93, 61.8) * mm});
            skLineSegment(sketch, "E746.MirrorCS", {"start": v(324.28, 58.31) * mm, "end": v(324.3, 57.55) * mm});
            skLineSegment(sketch, "E747.MirrorCS", {"start": v(221.38, 48.47) * mm, "end": v(221.39, 47.7) * mm});
            skLineSegment(sketch, "E748.MirrorCS", {"start": v(622.8, 54.05) * mm, "end": v(622.8, 53.29) * mm});
            skLineSegment(sketch, "E749.MirrorCS", {"start": v(321.15, 40.32) * mm, "end": v(321.14, 41.08) * mm});
            skLineSegment(sketch, "E750.MirrorCS", {"start": v(563.01, 43.58) * mm, "end": v(576.98, 43.68) * mm});
            skLineSegment(sketch, "E751.MirrorCS", {"start": v(563.02, 42.82) * mm, "end": v(563.03, 42.06) * mm});
            skLineSegment(sketch, "E752.MirrorCS", {"start": v(576.93, 61.8) * mm, "end": v(576.91, 62.56) * mm});
            skLineSegment(sketch, "E753.MirrorCS", {"start": v(380.44, 60.02) * mm, "end": v(380.45, 59.26) * mm});
            skLineSegment(sketch, "E754.MirrorCS", {"start": v(407.67, 51.47) * mm, "end": v(407.68, 50.7) * mm});
            skLineSegment(sketch, "E755.MirrorCS", {"start": v(460.79, 42.08) * mm, "end": v(460.8, 41.32) * mm});
            skLineSegment(sketch, "E756.MirrorCS", {"start": v(383.67, 41.53) * mm, "end": v(383.67, 42.3) * mm});
            skLineSegment(sketch, "E757.MirrorCS", {"start": v(563.03, 42.06) * mm, "end": v(576.99, 42.16) * mm});
            skLineSegment(sketch, "E758.MirrorCS", {"start": v(580.09, 62.61) * mm, "end": v(580.1, 61.85) * mm});
            skLineSegment(sketch, "E759.MirrorCS", {"start": v(480.44, 60.17) * mm, "end": v(480.43, 60.94) * mm});
            skLineSegment(sketch, "E760.MirrorCS", {"start": v(525.57, 61.7) * mm, "end": v(525.56, 62.46) * mm});
            skLineSegment(sketch, "E761.MirrorCS", {"start": v(505.2, 61.35) * mm, "end": v(505.18, 62.11) * mm});
            skLineSegment(sketch, "E762.MirrorCS", {"start": v(407.7, 49.95) * mm, "end": v(407.68, 50.7) * mm});
            skLineSegment(sketch, "E763.MirrorCS", {"start": v(254.52, 48.1) * mm, "end": v(254.51, 48.87) * mm});
            skLineSegment(sketch, "E764.MirrorCS", {"start": v(593.12, 53.7) * mm, "end": v(593.13, 52.93) * mm});
            skLineSegment(sketch, "E765.MirrorCS", {"start": v(611.58, 52.4) * mm, "end": v(622.81, 52.53) * mm});
            skLineSegment(sketch, "E766.MirrorCS", {"start": v(380.5, 42.27) * mm, "end": v(380.5, 41.5) * mm});
            skLineSegment(sketch, "E767.MirrorCS", {"start": v(576.99, 42.16) * mm, "end": v(576.98, 42.92) * mm});
            skLineSegment(sketch, "E768.MirrorCS", {"start": v(179.73, 55.12) * mm, "end": v(179.72, 55.88) * mm});
            skLineSegment(sketch, "E769.MirrorCS", {"start": v(142.14, 55.25) * mm, "end": v(142.16, 54.5) * mm});
            skLineSegment(sketch, "E770.MirrorCS", {"start": v(433.37, 42.65) * mm, "end": v(433.38, 41.89) * mm});
            skLineSegment(sketch, "E771.MirrorCS", {"start": v(541.7, 41.9) * mm, "end": v(541.69, 42.67) * mm});
            skLineSegment(sketch, "E772.MirrorCS", {"start": v(596.3, 53.73) * mm, "end": v(608.38, 53.88) * mm});
            skLineSegment(sketch, "E773.MirrorCS", {"start": v(433.31, 60.9) * mm, "end": v(433.33, 60.14) * mm});
            skLineSegment(sketch, "E774.MirrorCS", {"start": v(580.14, 52.02) * mm, "end": v(593.14, 52.17) * mm});
            skLineSegment(sketch, "E775.MirrorCS", {"start": v(544.8, 62.02) * mm, "end": v(544.79, 62.78) * mm});
            skLineSegment(sketch, "E776.MirrorCS", {"start": v(544.8, 62.02) * mm, "end": v(544.81, 61.26) * mm});
            skLineSegment(sketch, "E777.MirrorCS", {"start": v(580.08, 63.37) * mm, "end": v(593.07, 63.6) * mm});
            skLineSegment(sketch, "E778.MirrorCS", {"start": v(596.31, 52.2) * mm, "end": v(608.4, 52.35) * mm});
            skLineSegment(sketch, "E779.MirrorCS", {"start": v(580.13, 52.78) * mm, "end": v(580.12, 53.54) * mm});
            skLineSegment(sketch, "E780.MirrorCS", {"start": v(138.97, 48.25) * mm, "end": v(138.98, 47.48) * mm});
            skLineSegment(sketch, "E781.MirrorCS", {"start": v(505.23, 51.88) * mm, "end": v(505.24, 51.12) * mm});
            skLineSegment(sketch, "E782.MirrorCS", {"start": v(483.66, 42.25) * mm, "end": v(483.65, 43.01) * mm});
            skLineSegment(sketch, "E783.MirrorCS", {"start": v(562.95, 62.32) * mm, "end": v(562.94, 63.08) * mm});
            skLineSegment(sketch, "E784.MirrorCS", {"start": v(562.94, 63.08) * mm, "end": v(576.9, 63.32) * mm});
            skLineSegment(sketch, "E785.MirrorCS", {"start": v(321.12, 57.5) * mm, "end": v(321.1, 58.26) * mm});
            skLineSegment(sketch, "E786.MirrorCS", {"start": v(457.57, 59.79) * mm, "end": v(457.56, 60.55) * mm});
            skLineSegment(sketch, "E787.MirrorCS", {"start": v(505.23, 51.88) * mm, "end": v(505.22, 52.64) * mm});
            skLineSegment(sketch, "E788.MirrorCS", {"start": v(541.68, 43.43) * mm, "end": v(541.69, 42.67) * mm});
            skLineSegment(sketch, "E789.MirrorCS", {"start": v(321.14, 41.84) * mm, "end": v(321.14, 41.08) * mm});
            skLineSegment(sketch, "E790.MirrorCS", {"start": v(502.07, 43.14) * mm, "end": v(502.08, 42.38) * mm});
            skLineSegment(sketch, "E791.MirrorCS", {"start": v(436.55, 41.9) * mm, "end": v(436.56, 41.15) * mm});
            skLineSegment(sketch, "E792.MirrorCS", {"start": v(596.3, 52.97) * mm, "end": v(596.31, 52.2) * mm});
            skLineSegment(sketch, "E793.MirrorCS", {"start": v(559.77, 63.03) * mm, "end": v(559.78, 62.27) * mm});
            skLineSegment(sketch, "E794.MirrorCS", {"start": v(457.55, 61.31) * mm, "end": v(457.56, 60.55) * mm});
            skLineSegment(sketch, "E795.MirrorCS", {"start": v(559.8, 61.5) * mm, "end": v(559.78, 62.27) * mm});
            skLineSegment(sketch, "E796.MirrorCS", {"start": v(460.79, 42.08) * mm, "end": v(460.78, 42.85) * mm});
            skLineSegment(sketch, "E797.MirrorCS", {"start": v(544.86, 42.69) * mm, "end": v(544.87, 41.93) * mm});
            skLineSegment(sketch, "E798.MirrorCS", {"start": v(544.86, 42.69) * mm, "end": v(544.86, 43.45) * mm});
            skLineSegment(sketch, "E799.MirrorCS", {"start": v(288.8, 40.08) * mm, "end": v(288.8, 40.85) * mm});
            skLineSegment(sketch, "E800.MirrorCS", {"start": v(433.38, 41.13) * mm, "end": v(433.38, 41.89) * mm});
            skLineSegment(sketch, "E801.MirrorCS", {"start": v(593.14, 52.17) * mm, "end": v(593.13, 52.93) * mm});
            skLineSegment(sketch, "E802.MirrorCS", {"start": v(596.3, 52.97) * mm, "end": v(596.3, 53.73) * mm});
            skLineSegment(sketch, "E803.MirrorCS", {"start": v(321.1, 59.02) * mm, "end": v(321.1, 58.26) * mm});
            skLineSegment(sketch, "E804.MirrorCS", {"start": v(502, 62.06) * mm, "end": v(502.02, 61.3) * mm});
            skLineSegment(sketch, "E805.MirrorCS", {"start": v(505.25, 42.4) * mm, "end": v(505.26, 41.64) * mm});
            skLineSegment(sketch, "E806.MirrorCS", {"start": v(50.06, 32.6) * mm, "end": v(50.06, 31.84) * mm});
            skLineSegment(sketch, "E807.MirrorCS", {"start": v(596.34, 42.3) * mm, "end": v(608.43, 42.39) * mm});
            skLineSegment(sketch, "E808.MirrorCS", {"start": v(611.56, 53.92) * mm, "end": v(622.8, 54.05) * mm});
            skLineSegment(sketch, "E809.MirrorCS", {"start": v(457.58, 52.07) * mm, "end": v(457.59, 51.3) * mm});
            skLineSegment(sketch, "E810.MirrorCS", {"start": v(483.6, 60.99) * mm, "end": v(483.6, 61.75) * mm});
            skLineSegment(sketch, "E811.MirrorCS", {"start": v(257.67, 57.2) * mm, "end": v(257.68, 56.43) * mm});
            skLineSegment(sketch, "E812.MirrorCS", {"start": v(593.15, 43.8) * mm, "end": v(593.16, 43.04) * mm});
            skLineSegment(sketch, "E813.MirrorCS", {"start": v(254.5, 49.63) * mm, "end": v(254.51, 48.87) * mm});
            skLineSegment(sketch, "E814.MirrorCS", {"start": v(563, 51.8) * mm, "end": v(576.96, 51.98) * mm});
            skLineSegment(sketch, "E815.MirrorCS", {"start": v(138.99, 46.72) * mm, "end": v(138.98, 47.48) * mm});
            skLineSegment(sketch, "E816.MirrorCS", {"start": v(525.57, 61.7) * mm, "end": v(525.58, 60.93) * mm});
            skLineSegment(sketch, "E817.MirrorCS", {"start": v(291.98, 32.42) * mm, "end": v(291.98, 33.18) * mm});
            skLineSegment(sketch, "E818.MirrorCS", {"start": v(354.85, 41.32) * mm, "end": v(354.85, 42.08) * mm});
            skLineSegment(sketch, "E819.MirrorCS", {"start": v(457.6, 50.54) * mm, "end": v(457.59, 51.3) * mm});
            skLineSegment(sketch, "E820.MirrorCS", {"start": v(611.53, 63.14) * mm, "end": v(611.54, 62.38) * mm});
            skLineSegment(sketch, "E821.MirrorCS", {"start": v(218.22, 33) * mm, "end": v(218.22, 32.24) * mm});
            skLineSegment(sketch, "E822.MirrorCS", {"start": v(383.67, 41.53) * mm, "end": v(383.68, 40.77) * mm});
            skLineSegment(sketch, "E823.MirrorCS", {"start": v(562.98, 53.33) * mm, "end": v(576.94, 53.5) * mm});
            skLineSegment(sketch, "E824.MirrorCS", {"start": v(563, 52.57) * mm, "end": v(562.98, 53.33) * mm});
            skLineSegment(sketch, "E825.MirrorCS", {"start": v(480.42, 61.7) * mm, "end": v(480.43, 60.94) * mm});
            skLineSegment(sketch, "E826.MirrorCS", {"start": v(580.16, 42.94) * mm, "end": v(580.15, 43.7) * mm});
            skLineSegment(sketch, "E827.MirrorCS", {"start": v(380.5, 40.74) * mm, "end": v(380.5, 41.5) * mm});
            skLineSegment(sketch, "E828.MirrorCS", {"start": v(221.4, 32.25) * mm, "end": v(221.4, 33.01) * mm});
            skLineSegment(sketch, "E829.MirrorCS", {"start": v(138.96, 55.96) * mm, "end": v(138.97, 55.2) * mm});
            skLineSegment(sketch, "E830.MirrorCS", {"start": v(593.16, 42.28) * mm, "end": v(593.16, 43.04) * mm});
            skLineSegment(sketch, "E831.MirrorCS", {"start": v(288.8, 31.65) * mm, "end": v(288.8, 32.41) * mm});
            skLineSegment(sketch, "E832.MirrorCS", {"start": v(580.16, 42.18) * mm, "end": v(593.16, 42.28) * mm});
            skLineSegment(sketch, "E833.MirrorCS", {"start": v(410.83, 59.77) * mm, "end": v(410.82, 60.53) * mm});
            skLineSegment(sketch, "E834.MirrorCS", {"start": v(354.81, 58.83) * mm, "end": v(354.83, 58.06) * mm});
            skLineSegment(sketch, "E835.MirrorCS", {"start": v(351.63, 59.53) * mm, "end": v(351.64, 58.77) * mm});
            skLineSegment(sketch, "E836.MirrorCS", {"start": v(257.7, 32.34) * mm, "end": v(257.7, 31.57) * mm});
            skLineSegment(sketch, "E837.MirrorCS", {"start": v(257.7, 32.34) * mm, "end": v(257.7, 33.1) * mm});
            skLineSegment(sketch, "E838.MirrorCS", {"start": v(460.73, 60.6) * mm, "end": v(460.75, 59.84) * mm});
            skLineSegment(sketch, "E839.MirrorCS", {"start": v(254.48, 57.9) * mm, "end": v(254.5, 57.14) * mm});
            skLineSegment(sketch, "E840.MirrorCS", {"start": v(221.4, 32.25) * mm, "end": v(221.4, 31.49) * mm});
            skLineSegment(sketch, "E841.MirrorCS", {"start": v(611.51, 63.9) * mm, "end": v(622.75, 64.09) * mm});
            skLineSegment(sketch, "E842.MirrorCS", {"start": v(351.65, 58.01) * mm, "end": v(351.64, 58.77) * mm});
            skLineSegment(sketch, "E843.MirrorCS", {"start": v(254.53, 31.57) * mm, "end": v(254.53, 32.33) * mm});
            skLineSegment(sketch, "E844.MirrorCS", {"start": v(138.98, 54.44) * mm, "end": v(138.97, 55.2) * mm});
            skLineSegment(sketch, "E845.MirrorCS", {"start": v(580.15, 43.7) * mm, "end": v(593.15, 43.8) * mm});
            skLineSegment(sketch, "E846.MirrorCS", {"start": v(460.73, 60.6) * mm, "end": v(460.72, 61.37) * mm});
            skLineSegment(sketch, "E847.MirrorCS", {"start": v(433.34, 59.38) * mm, "end": v(433.33, 60.14) * mm});
            skLineSegment(sketch, "E848.MirrorCS", {"start": v(288.78, 56.95) * mm, "end": v(288.76, 57.72) * mm});
            skLineSegment(sketch, "E849.MirrorCS", {"start": v(541.64, 61.2) * mm, "end": v(541.63, 61.96) * mm});
            skLineSegment(sketch, "E850.MirrorCS", {"start": v(288.75, 58.48) * mm, "end": v(288.76, 57.72) * mm});
            skLineSegment(sketch, "E851.MirrorCS", {"start": v(221.36, 56.58) * mm, "end": v(221.35, 57.34) * mm});
            skLineSegment(sketch, "E852.MirrorCS", {"start": v(541.61, 62.73) * mm, "end": v(541.63, 61.96) * mm});
            skLineSegment(sketch, "E853.MirrorCS", {"start": v(410.83, 59.77) * mm, "end": v(410.84, 59) * mm});
            skLineSegment(sketch, "E854.MirrorCS", {"start": v(622.77, 62.57) * mm, "end": v(622.76, 63.33) * mm});
            skLineSegment(sketch, "E855.MirrorCS", {"start": v(407.67, 58.95) * mm, "end": v(407.65, 59.71) * mm});
            skLineSegment(sketch, "E856.MirrorCS", {"start": v(611.54, 62.38) * mm, "end": v(622.77, 62.57) * mm});
            skLineSegment(sketch, "E857.MirrorCS", {"start": v(254.5, 56.38) * mm, "end": v(254.5, 57.14) * mm});
            skLineSegment(sketch, "E858.MirrorCS", {"start": v(254.53, 33.1) * mm, "end": v(254.53, 32.33) * mm});
            skLineSegment(sketch, "E859.MirrorCS", {"start": v(354.81, 58.83) * mm, "end": v(354.8, 59.59) * mm});
            skLineSegment(sketch, "E860.MirrorCS", {"start": v(407.64, 60.47) * mm, "end": v(407.65, 59.71) * mm});
            skLineSegment(sketch, "E861.MirrorCS", {"start": v(622.75, 64.09) * mm, "end": v(622.76, 63.33) * mm});
            skLineSegment(sketch, "E862.MirrorCS", {"start": v(221.36, 56.58) * mm, "end": v(221.38, 55.82) * mm});
            skLineSegment(sketch, "E863.MirrorCS", {"start": v(288.8, 33.17) * mm, "end": v(288.8, 32.41) * mm});
            skLineSegment(sketch, "E864.MirrorCS", {"start": v(407.7, 33.46) * mm, "end": v(407.7, 32.7) * mm});
            skLineSegment(sketch, "E865.MirrorCS", {"start": v(324.33, 32.5) * mm, "end": v(324.33, 33.26) * mm});
            skLineSegment(sketch, "E866.MirrorCS", {"start": v(182.91, 47.25) * mm, "end": v(218.21, 47.67) * mm, "construction": true});
            skLineSegment(sketch, "E867.MirrorCS", {"start": v(354.86, 32.57) * mm, "end": v(354.86, 31.8) * mm});
            skLineSegment(sketch, "E868.MirrorCS", {"start": v(351.69, 31.8) * mm, "end": v(351.69, 32.56) * mm});
            skLineSegment(sketch, "E869.MirrorCS", {"start": v(383.68, 32.64) * mm, "end": v(383.68, 33.4) * mm});
            skLineSegment(sketch, "E870.MirrorCS", {"start": v(324.33, 32.5) * mm, "end": v(324.33, 31.73) * mm});
            skLineSegment(sketch, "E871.MirrorCS", {"start": v(291.97, 48.56) * mm, "end": v(321.14, 48.9) * mm});
            skLineSegment(sketch, "E872.MirrorCS", {"start": v(321.15, 33.25) * mm, "end": v(321.15, 32.49) * mm});
            skLineSegment(sketch, "E873.MirrorCS", {"start": v(182.92, 39.32) * mm, "end": v(218.22, 39.58) * mm, "construction": true});
            skLineSegment(sketch, "E874.MirrorCS", {"start": v(324.3, 50.47) * mm, "end": v(351.65, 50.8) * mm});
            skLineSegment(sketch, "E875.MirrorCS", {"start": v(4.75, 53.7) * mm, "end": v(50.04, 54.47) * mm});
            skLineSegment(sketch, "E876.MirrorCS", {"start": v(182.9, 48.77) * mm, "end": v(218.2, 49.2) * mm, "construction": true});
            skLineSegment(sketch, "E877.MirrorCS", {"start": v(257.7, 48.15) * mm, "end": v(288.8, 48.52) * mm});
            skLineSegment(sketch, "E878.MirrorCS", {"start": v(53.21, 54.52) * mm, "end": v(95.78, 55.24) * mm});
            skLineSegment(sketch, "E879.MirrorCS", {"start": v(182.91, 32.92) * mm, "end": v(218.22, 33) * mm, "construction": true});
            skLineSegment(sketch, "E880.MirrorCS", {"start": v(354.86, 32.57) * mm, "end": v(354.86, 33.33) * mm});
            skLineSegment(sketch, "E881.MirrorCS", {"start": v(182.9, 55.17) * mm, "end": v(218.2, 55.77) * mm, "construction": true});
            skLineSegment(sketch, "E882.MirrorCS", {"start": v(182.9, 40.85) * mm, "end": v(218.2, 41.1) * mm, "construction": true});
            skLineSegment(sketch, "E883.MirrorCS", {"start": v(351.68, 33.32) * mm, "end": v(351.69, 32.56) * mm});
            skLineSegment(sketch, "E884.MirrorCS", {"start": v(182.92, 31.4) * mm, "end": v(218.22, 31.48) * mm, "construction": true});
            skLineSegment(sketch, "E885.MirrorCS", {"start": v(354.85, 49.31) * mm, "end": v(380.5, 49.62) * mm});
            skLineSegment(sketch, "E886.MirrorCS", {"start": v(410.88, 32.7) * mm, "end": v(410.88, 33.47) * mm});
            skLineSegment(sketch, "E887.MirrorCS", {"start": v(380.5, 33.4) * mm, "end": v(380.5, 32.63) * mm});
            skLineSegment(sketch, "E888.MirrorCS", {"start": v(321.15, 31.73) * mm, "end": v(321.15, 32.49) * mm});
            skLineSegment(sketch, "E889.MirrorCS", {"start": v(291.98, 31.66) * mm, "end": v(321.15, 31.73) * mm});
            skLineSegment(sketch, "E890.MirrorCS", {"start": v(436.54, 50.3) * mm, "end": v(457.6, 50.54) * mm});
            skLineSegment(sketch, "E891.MirrorCS", {"start": v(4.76, 39.56) * mm, "end": v(50.05, 39.89) * mm});
            skLineSegment(sketch, "E892.MirrorCS", {"start": v(354.86, 40.56) * mm, "end": v(380.5, 40.74) * mm});
            skLineSegment(sketch, "E893.MirrorCS", {"start": v(544.85, 51.6) * mm, "end": v(559.83, 51.77) * mm});
            skLineSegment(sketch, "E894.MirrorCS", {"start": v(544.86, 43.45) * mm, "end": v(559.84, 43.56) * mm});
            skLineSegment(sketch, "E895.MirrorCS", {"start": v(53.23, 39.91) * mm, "end": v(95.8, 40.22) * mm});
            skLineSegment(sketch, "E896.MirrorCS", {"start": v(483.67, 41.49) * mm, "end": v(502.08, 41.62) * mm});
            skLineSegment(sketch, "E897.MirrorCS", {"start": v(53.24, 45.7) * mm, "end": v(95.8, 46.2) * mm});
            skLineSegment(sketch, "E898.MirrorCS", {"start": v(354.83, 58.06) * mm, "end": v(380.47, 58.5) * mm});
            skLineSegment(sketch, "E899.MirrorCS", {"start": v(324.33, 33.26) * mm, "end": v(351.68, 33.32) * mm});
            skLineSegment(sketch, "E900.MirrorCS", {"start": v(142.16, 40.55) * mm, "end": v(179.73, 40.82) * mm});
            skLineSegment(sketch, "E901.MirrorCS", {"start": v(182.92, 39.32) * mm, "end": v(218.22, 39.58) * mm});
            skLineSegment(sketch, "E902.MirrorCS", {"start": v(460.76, 52.1) * mm, "end": v(480.45, 52.34) * mm});
            skLineSegment(sketch, "E903.MirrorCS", {"start": v(410.87, 49.98) * mm, "end": v(433.37, 50.25) * mm});
            skLineSegment(sketch, "E904.MirrorCS", {"start": v(544.79, 62.78) * mm, "end": v(559.77, 63.03) * mm});
            skLineSegment(sketch, "E905.MirrorCS", {"start": v(483.62, 60.23) * mm, "end": v(502.03, 60.54) * mm});
            skLineSegment(sketch, "E906.MirrorCS", {"start": v(460.8, 33.59) * mm, "end": v(480.5, 33.63) * mm});
            skLineSegment(sketch, "E907.MirrorCS", {"start": v(257.7, 31.57) * mm, "end": v(288.8, 31.65) * mm});
            skLineSegment(sketch, "E908.MirrorCS", {"start": v(142.17, 39.03) * mm, "end": v(179.74, 39.3) * mm});
            skLineSegment(sketch, "E909.MirrorCS", {"start": v(182.9, 48.77) * mm, "end": v(218.2, 49.2) * mm});
            skLineSegment(sketch, "E910.MirrorCS", {"start": v(525.61, 51.36) * mm, "end": v(541.67, 51.55) * mm});
            skLineSegment(sketch, "E911.MirrorCS", {"start": v(182.9, 55.17) * mm, "end": v(218.2, 55.77) * mm});
            skLineSegment(sketch, "E912.MirrorCS", {"start": v(182.91, 32.92) * mm, "end": v(218.22, 33) * mm});
            skLineSegment(sketch, "E913.MirrorCS", {"start": v(525.62, 43.31) * mm, "end": v(541.68, 43.43) * mm});
            skLineSegment(sketch, "E914.MirrorCS", {"start": v(505.24, 51.12) * mm, "end": v(522.44, 51.32) * mm});
            skLineSegment(sketch, "E915.MirrorCS", {"start": v(257.68, 49.67) * mm, "end": v(288.77, 50.04) * mm});
            skLineSegment(sketch, "E916.MirrorCS", {"start": v(221.38, 41.12) * mm, "end": v(254.52, 41.36) * mm});
            skLineSegment(sketch, "E917.MirrorCS", {"start": v(324.3, 57.55) * mm, "end": v(351.65, 58.01) * mm});
            skLineSegment(sketch, "E918.MirrorCS", {"start": v(291.92, 58.53) * mm, "end": v(321.1, 59.02) * mm});
            skLineSegment(sketch, "E919.MirrorCS", {"start": v(383.66, 49.66) * mm, "end": v(407.7, 49.95) * mm});
            skLineSegment(sketch, "E920.MirrorCS", {"start": v(221.39, 47.7) * mm, "end": v(254.52, 48.1) * mm});
            skLineSegment(sketch, "E921.MirrorCS", {"start": v(483.63, 52.38) * mm, "end": v(502.04, 52.6) * mm});
            skLineSegment(sketch, "E922.MirrorCS", {"start": v(383.67, 42.3) * mm, "end": v(407.7, 42.46) * mm});
            skLineSegment(sketch, "E923.MirrorCS", {"start": v(4.77, 45.11) * mm, "end": v(50.06, 45.65) * mm});
            skLineSegment(sketch, "E924.MirrorCS", {"start": v(505.22, 52.64) * mm, "end": v(522.42, 52.85) * mm});
            skLineSegment(sketch, "E925.MirrorCS", {"start": v(460.8, 41.32) * mm, "end": v(480.5, 41.46) * mm});
            skLineSegment(sketch, "E926.MirrorCS", {"start": v(324.33, 40.34) * mm, "end": v(351.68, 40.54) * mm});
            skLineSegment(sketch, "E927.MirrorCS", {"start": v(410.85, 51.5) * mm, "end": v(433.35, 51.78) * mm});
            skLineSegment(sketch, "E928.MirrorCS", {"start": v(291.97, 41.63) * mm, "end": v(321.14, 41.84) * mm});
            skLineSegment(sketch, "E929.MirrorCS", {"start": v(505.26, 33.7) * mm, "end": v(522.46, 33.73) * mm});
            skLineSegment(sketch, "E930.MirrorCS", {"start": v(0, 52.86) * mm, "end": v(648.16, 63.75) * mm, "construction": true});
            skLineSegment(sketch, "E931.MirrorCS", {"start": v(4.77, 52.18) * mm, "end": v(50.06, 52.94) * mm});
            skLineSegment(sketch, "E932.MirrorCS", {"start": v(53.24, 53) * mm, "end": v(95.8, 53.71) * mm});
            skLineSegment(sketch, "E933.MirrorCS", {"start": v(142.16, 54.5) * mm, "end": v(179.73, 55.12) * mm});
            skLineSegment(sketch, "E934.MirrorCS", {"start": v(460.78, 42.85) * mm, "end": v(480.48, 42.99) * mm});
            skLineSegment(sketch, "E935.MirrorCS", {"start": v(257.7, 39.86) * mm, "end": v(288.8, 40.08) * mm});
            skLineSegment(sketch, "E936.MirrorCS", {"start": v(410.88, 40.96) * mm, "end": v(433.38, 41.13) * mm});
            skLineSegment(sketch, "E937.MirrorCS", {"start": v(142.15, 48.28) * mm, "end": v(179.72, 48.73) * mm});
            skLineSegment(sketch, "E938.MirrorCS", {"start": v(182.91, 47.25) * mm, "end": v(218.21, 47.67) * mm});
            skLineSegment(sketch, "E939.MirrorCS", {"start": v(324.27, 59.07) * mm, "end": v(351.63, 59.53) * mm});
            skLineSegment(sketch, "E940.MirrorCS", {"start": v(182.88, 56.7) * mm, "end": v(218.18, 57.3) * mm, "construction": true});
            skLineSegment(sketch, "E941.MirrorCS", {"start": v(142.16, 46.76) * mm, "end": v(179.74, 47.21) * mm});
            skLineSegment(sketch, "E942.MirrorCS", {"start": v(436.55, 42.67) * mm, "end": v(457.6, 42.82) * mm});
            skLineSegment(sketch, "E943.MirrorCS", {"start": v(257.68, 56.43) * mm, "end": v(288.78, 56.95) * mm});
            skLineSegment(sketch, "E944.MirrorCS", {"start": v(354.83, 50.84) * mm, "end": v(380.47, 51.14) * mm});
            skLineSegment(sketch, "E945.MirrorCS", {"start": v(291.98, 40.1) * mm, "end": v(321.15, 40.32) * mm});
            skLineSegment(sketch, "E946.MirrorCS", {"start": v(436.56, 41.15) * mm, "end": v(457.62, 41.3) * mm});
            skLineSegment(sketch, "E947.MirrorCS", {"start": v(182.9, 40.85) * mm, "end": v(218.2, 41.1) * mm});
            skLineSegment(sketch, "E948.MirrorCS", {"start": v(221.35, 57.34) * mm, "end": v(254.48, 57.9) * mm});
            skLineSegment(sketch, "E949.MirrorCS", {"start": v(525.63, 41.79) * mm, "end": v(541.7, 41.9) * mm});
            skLineSegment(sketch, "E950.MirrorCS", {"start": v(436.52, 51.82) * mm, "end": v(457.58, 52.07) * mm});
            skLineSegment(sketch, "E951.MirrorCS", {"start": v(98.97, 40.24) * mm, "end": v(138.98, 40.53) * mm});
            skLineSegment(sketch, "E952.MirrorCS", {"start": v(544.87, 41.93) * mm, "end": v(559.85, 42.04) * mm});
            skLineSegment(sketch, "E953.MirrorCS", {"start": v(4.75, 46.63) * mm, "end": v(50.05, 47.18) * mm});
            skLineSegment(sketch, "E954.MirrorCS", {"start": v(-33.04, 56.39) * mm, "end": v(118.54, 56.39) * mm, "construction": true});
            skLineSegment(sketch, "E955.MirrorCS", {"start": v(525.56, 62.46) * mm, "end": v(541.61, 62.73) * mm});
            skLineSegment(sketch, "E956.MirrorCS", {"start": v(291.95, 57) * mm, "end": v(321.12, 57.5) * mm});
            skLineSegment(sketch, "E957.MirrorCS", {"start": v(436.51, 59.44) * mm, "end": v(457.57, 59.79) * mm});
            skLineSegment(sketch, "E958.MirrorCS", {"start": v(53.23, 32.6) * mm, "end": v(95.8, 32.71) * mm});
            skLineSegment(sketch, "E959.MirrorCS", {"start": v(483.67, 32.12) * mm, "end": v(502.09, 32.16) * mm});
            skLineSegment(sketch, "E960.MirrorCS", {"start": v(324.31, 41.86) * mm, "end": v(351.67, 42.06) * mm});
            skLineSegment(sketch, "E961.MirrorCS", {"start": v(53.22, 47.22) * mm, "end": v(95.8, 47.73) * mm});
            skLineSegment(sketch, "E962.MirrorCS", {"start": v(53.24, 38.39) * mm, "end": v(95.81, 38.7) * mm});
            skLineSegment(sketch, "E963.MirrorCS", {"start": v(544.83, 53.12) * mm, "end": v(559.8, 53.3) * mm});
            skLineSegment(sketch, "E964.MirrorCS", {"start": v(483.65, 50.86) * mm, "end": v(502.06, 51.08) * mm});
            skLineSegment(sketch, "E965.MirrorCS", {"start": v(544.81, 61.26) * mm, "end": v(559.8, 61.5) * mm});
            skLineSegment(sketch, "E966.MirrorCS", {"start": v(4.77, 38.04) * mm, "end": v(50.06, 38.37) * mm});
            skLineSegment(sketch, "E967.MirrorCS", {"start": v(291.95, 50.08) * mm, "end": v(321.12, 50.43) * mm});
            skLineSegment(sketch, "E968.MirrorCS", {"start": v(324.31, 48.95) * mm, "end": v(351.67, 49.27) * mm});
            skLineSegment(sketch, "E969.MirrorCS", {"start": v(460.77, 50.58) * mm, "end": v(480.47, 50.82) * mm});
            skLineSegment(sketch, "E970.MirrorCS", {"start": v(525.58, 60.93) * mm, "end": v(541.64, 61.2) * mm});
            skLineSegment(sketch, "E971.MirrorCS", {"start": v(291.98, 33.18) * mm, "end": v(321.15, 33.25) * mm});
            skLineSegment(sketch, "E972.MirrorCS", {"start": v(505.25, 43.17) * mm, "end": v(522.45, 43.3) * mm});
            skLineSegment(sketch, "E973.MirrorCS", {"start": v(410.87, 42.49) * mm, "end": v(433.37, 42.65) * mm});
            skLineSegment(sketch, "E974.MirrorCS", {"start": v(383.65, 51.18) * mm, "end": v(407.67, 51.47) * mm});
            skLineSegment(sketch, "E975.MirrorCS", {"start": v(505.18, 62.11) * mm, "end": v(522.38, 62.4) * mm});
            skLineSegment(sketch, "E976.MirrorCS", {"start": v(383.68, 33.4) * mm, "end": v(407.7, 33.46) * mm});
            skLineSegment(sketch, "E977.MirrorCS", {"start": v(483.65, 43.01) * mm, "end": v(502.07, 43.14) * mm});
            skLineSegment(sketch, "E978.MirrorCS", {"start": v(221.4, 39.6) * mm, "end": v(254.53, 39.84) * mm});
            skLineSegment(sketch, "E979.MirrorCS", {"start": v(383.68, 40.77) * mm, "end": v(407.7, 40.94) * mm});
            skLineSegment(sketch, "E980.MirrorCS", {"start": v(98.98, 46.24) * mm, "end": v(138.99, 46.72) * mm});
            skLineSegment(sketch, "E981.MirrorCS", {"start": v(221.38, 55.82) * mm, "end": v(254.5, 56.38) * mm});
            skLineSegment(sketch, "E982.MirrorCS", {"start": v(525.6, 52.88) * mm, "end": v(541.65, 53.08) * mm});
            skLineSegment(sketch, "E983.MirrorCS", {"start": v(257.7, 41.38) * mm, "end": v(288.8, 41.6) * mm});
            skLineSegment(sketch, "E984.MirrorCS", {"start": v(505.26, 41.64) * mm, "end": v(522.46, 41.77) * mm});
            skLineSegment(sketch, "E985.MirrorCS", {"start": v(221.37, 49.23) * mm, "end": v(254.5, 49.63) * mm});
            skLineSegment(sketch, "E986.MirrorCS", {"start": v(257.66, 57.95) * mm, "end": v(288.75, 58.48) * mm});
            skLineSegment(sketch, "E987.MirrorCS", {"start": v(505.2, 60.6) * mm, "end": v(522.4, 60.88) * mm});
            skLineSegment(sketch, "E988.MirrorCS", {"start": v(0, 38.77) * mm, "end": v(648.23, 43.43) * mm, "construction": true});
            skLineSegment(sketch, "E989.MirrorCS", {"start": v(354.85, 42.08) * mm, "end": v(380.5, 42.27) * mm});
            skLineSegment(sketch, "E990.MirrorCS", {"start": v(98.98, 32.72) * mm, "end": v(138.99, 32.81) * mm});
            skLineSegment(sketch, "E991.MirrorCS", {"start": v(98.97, 47.76) * mm, "end": v(138.97, 48.25) * mm});
            skLineSegment(sketch, "E992.MirrorCS", {"start": v(354.8, 59.59) * mm, "end": v(380.44, 60.02) * mm});
            skLineSegment(sketch, "E993.MirrorCS", {"start": v(53.23, 31.08) * mm, "end": v(95.8, 31.19) * mm});
            skLineSegment(sketch, "E994.MirrorCS", {"start": v(460.8, 32.82) * mm, "end": v(460.8, 33.59) * mm});
            skLineSegment(sketch, "E995.MirrorCS", {"start": v(433.38, 33.52) * mm, "end": v(433.39, 32.76) * mm});
            skLineSegment(sketch, "E996.MirrorCS", {"start": v(142.13, 56.01) * mm, "end": v(179.7, 56.65) * mm});
            skLineSegment(sketch, "E997.MirrorCS", {"start": v(436.56, 32.77) * mm, "end": v(436.56, 33.53) * mm});
            skLineSegment(sketch, "E998.MirrorCS", {"start": v(354.86, 33.33) * mm, "end": v(380.5, 33.4) * mm});
            skLineSegment(sketch, "E999.MirrorCS", {"start": v(383.62, 60.07) * mm, "end": v(407.64, 60.47) * mm});
            skLineSegment(sketch, "E1000.MirrorCS", {"start": v(0, 45.05) * mm, "end": v(642.94, 52.77) * mm, "construction": true});
            skLineSegment(sketch, "E1001.MirrorCS", {"start": v(98.99, 38.72) * mm, "end": v(139, 39) * mm});
            skLineSegment(sketch, "E1002.MirrorCS", {"start": v(257.7, 33.1) * mm, "end": v(288.8, 33.17) * mm});
            skLineSegment(sketch, "E1003.MirrorCS", {"start": v(480.5, 33.63) * mm, "end": v(480.5, 32.87) * mm});
            skLineSegment(sketch, "E1004.MirrorCS", {"start": v(460.75, 59.84) * mm, "end": v(480.44, 60.17) * mm});
            skLineSegment(sketch, "E1005.MirrorCS", {"start": v(221.4, 31.49) * mm, "end": v(254.53, 31.57) * mm});
            skLineSegment(sketch, "E1006.MirrorCS", {"start": v(483.67, 33.64) * mm, "end": v(502.09, 33.69) * mm});
            skLineSegment(sketch, "E1007.MirrorCS", {"start": v(436.49, 60.96) * mm, "end": v(457.55, 61.31) * mm});
            skLineSegment(sketch, "E1008.MirrorCS", {"start": v(4.76, 30.97) * mm, "end": v(50.06, 31.08) * mm});
            skLineSegment(sketch, "E1009.MirrorCS", {"start": v(410.88, 33.47) * mm, "end": v(433.38, 33.52) * mm});
            skLineSegment(sketch, "E1010.MirrorCS", {"start": v(0, 52.1) * mm, "end": v(642.9, 62.9) * mm, "construction": true});
            skLineSegment(sketch, "E1011.MirrorCS", {"start": v(98.98, 53.76) * mm, "end": v(138.98, 54.44) * mm});
            skLineSegment(sketch, "E1012.MirrorCS", {"start": v(460.72, 61.37) * mm, "end": v(480.42, 61.7) * mm});
            skLineSegment(sketch, "E1013.MirrorCS", {"start": v(410.84, 59) * mm, "end": v(433.34, 59.38) * mm});
            skLineSegment(sketch, "E1014.MirrorCS", {"start": v(142.16, 32.82) * mm, "end": v(179.74, 32.91) * mm});
            skLineSegment(sketch, "E1015.MirrorCS", {"start": v(182.92, 31.4) * mm, "end": v(218.22, 31.48) * mm});
            skLineSegment(sketch, "E1016.MirrorCS", {"start": v(0, 45.82) * mm, "end": v(648.2, 53.6) * mm, "construction": true});
            skLineSegment(sketch, "E1017.MirrorCS", {"start": v(4.76, 32.5) * mm, "end": v(50.06, 32.6) * mm});
            skLineSegment(sketch, "E1018.MirrorCS", {"start": v(544.87, 33.79) * mm, "end": v(559.86, 33.82) * mm});
            skLineSegment(sketch, "E1019.MirrorCS", {"start": v(98.96, 55.29) * mm, "end": v(138.96, 55.96) * mm});
            skLineSegment(sketch, "E1020.MirrorCS", {"start": v(436.56, 33.53) * mm, "end": v(457.62, 33.58) * mm});
            skLineSegment(sketch, "E1021.MirrorCS", {"start": v(142.17, 31.3) * mm, "end": v(179.74, 31.39) * mm});
            skLineSegment(sketch, "E1022.MirrorCS", {"start": v(182.88, 56.7) * mm, "end": v(218.18, 57.3) * mm});
            skLineSegment(sketch, "E1023.MirrorCS", {"start": v(460.8, 32.06) * mm, "end": v(480.5, 32.1) * mm});
            skLineSegment(sketch, "E1024.MirrorCS", {"start": v(410.82, 60.53) * mm, "end": v(433.31, 60.9) * mm});
            skLineSegment(sketch, "E1025.MirrorCS", {"start": v(483.6, 61.75) * mm, "end": v(502, 62.06) * mm});
            skLineSegment(sketch, "E1026.MirrorCS", {"start": v(383.64, 58.55) * mm, "end": v(407.67, 58.95) * mm});
            skLineSegment(sketch, "E1027.MirrorCS", {"start": v(221.4, 33.01) * mm, "end": v(254.53, 33.1) * mm});
            skLineSegment(sketch, "E1028.MirrorCS", {"start": v(98.98, 31.2) * mm, "end": v(139, 31.29) * mm});
            skLineSegment(sketch, "E1029.MirrorCS", {"start": v(0, 38) * mm, "end": v(642.97, 42.63) * mm, "construction": true});
            skLineSegment(sketch, "E1030.MirrorCS", {"start": v(525.64, 33.74) * mm, "end": v(541.7, 33.78) * mm});
            skLineSegment(sketch, "E1031.MirrorCS", {"start": v(457.62, 33.58) * mm, "end": v(457.62, 32.82) * mm});
            skLineSegment(sketch, "E1032.MirrorCS", {"start": v(324.33, 31.73) * mm, "end": v(351.69, 31.8) * mm});
            skLineSegment(sketch, "E1033.MirrorCS", {"start": v(354.86, 31.8) * mm, "end": v(380.5, 31.87) * mm});
            skLineSegment(sketch, "E1034.MirrorCS", {"start": v(383.68, 32.64) * mm, "end": v(383.68, 31.88) * mm});
            skLineSegment(sketch, "E1035.MirrorCS", {"start": v(383.68, 31.88) * mm, "end": v(407.71, 31.93) * mm});
            skLineSegment(sketch, "E1036.MirrorCS", {"start": v(407.71, 31.93) * mm, "end": v(407.7, 32.7) * mm});
            skLineSegment(sketch, "E1037.MirrorCS", {"start": v(0, 30.96) * mm, "end": v(642.98, 32.5) * mm, "construction": true});
            skLineSegment(sketch, "E1038.MirrorCS", {"start": v(410.89, 31.94) * mm, "end": v(433.39, 32) * mm});
            skLineSegment(sketch, "E1039.MirrorCS", {"start": v(433.39, 32) * mm, "end": v(433.39, 32.76) * mm});
            skLineSegment(sketch, "E1040.MirrorCS", {"start": v(410.88, 32.7) * mm, "end": v(410.89, 31.94) * mm});
            skLineSegment(sketch, "E1041.MirrorCS", {"start": v(436.56, 32) * mm, "end": v(457.62, 32.05) * mm});
            skLineSegment(sketch, "E1042.MirrorCS", {"start": v(436.56, 32.77) * mm, "end": v(436.56, 32) * mm});
            skLineSegment(sketch, "E1043.MirrorCS", {"start": v(457.62, 32.05) * mm, "end": v(457.62, 32.82) * mm});
            skLineSegment(sketch, "E1044.MirrorCS", {"start": v(505.26, 32.17) * mm, "end": v(522.47, 32.21) * mm});
            skLineSegment(sketch, "E1045.MirrorCS", {"start": v(483.67, 32.88) * mm, "end": v(483.67, 32.12) * mm});
            skLineSegment(sketch, "E1046.MirrorCS", {"start": v(502.09, 32.16) * mm, "end": v(502.09, 32.92) * mm});
            skLineSegment(sketch, "E1047.MirrorCS", {"start": v(502.09, 33.69) * mm, "end": v(502.09, 32.92) * mm});
            skLineSegment(sketch, "E1048.MirrorCS", {"start": v(460.8, 32.82) * mm, "end": v(460.8, 32.06) * mm});
            skLineSegment(sketch, "E1049.MirrorCS", {"start": v(480.5, 32.1) * mm, "end": v(480.5, 32.87) * mm});
            skLineSegment(sketch, "E1050.MirrorCS", {"start": v(483.67, 32.88) * mm, "end": v(483.67, 33.64) * mm});
            skLineSegment(sketch, "E1051.MirrorCS", {"start": v(522.46, 33.73) * mm, "end": v(522.47, 32.97) * mm});
            skLineSegment(sketch, "E1052.MirrorCS", {"start": v(505.26, 32.93) * mm, "end": v(505.26, 33.7) * mm});
            skLineSegment(sketch, "E1053.MirrorCS", {"start": v(0, 31.72) * mm, "end": v(648.25, 33.27) * mm, "construction": true});
            skLineSegment(sketch, "E1054.MirrorCS", {"start": v(505.26, 32.93) * mm, "end": v(505.26, 32.17) * mm});
            skLineSegment(sketch, "E1055.MirrorCS", {"start": v(522.47, 32.21) * mm, "end": v(522.47, 32.97) * mm});
            skLineSegment(sketch, "E1056.MirrorCS", {"start": v(525.64, 32.98) * mm, "end": v(525.64, 32.22) * mm});
            skLineSegment(sketch, "E1057.MirrorCS", {"start": v(525.64, 32.98) * mm, "end": v(525.64, 33.74) * mm});
            skLineSegment(sketch, "E1058.MirrorCS", {"start": v(541.7, 32.26) * mm, "end": v(541.7, 33.02) * mm});
            skLineSegment(sketch, "E1059.MirrorCS", {"start": v(541.7, 33.78) * mm, "end": v(541.7, 33.02) * mm});
            skLineSegment(sketch, "E1060.MirrorCS", {"start": v(525.64, 32.22) * mm, "end": v(541.7, 32.26) * mm});
            skLineSegment(sketch, "E1061.MirrorCS", {"start": v(544.88, 33.03) * mm, "end": v(544.88, 32.26) * mm});
            skLineSegment(sketch, "E1062.MirrorCS", {"start": v(544.88, 32.26) * mm, "end": v(559.86, 32.3) * mm});
            skLineSegment(sketch, "E1063.MirrorCS", {"start": v(559.86, 32.3) * mm, "end": v(559.86, 33.06) * mm});
            skLineSegment(sketch, "E1064.MirrorCS", {"start": v(559.86, 33.82) * mm, "end": v(559.86, 33.06) * mm});
            skLineSegment(sketch, "E1065.MirrorCS", {"start": v(544.88, 33.03) * mm, "end": v(544.87, 33.79) * mm});
            skLineSegment(sketch, "E1066.MirrorCS", {"start": v(622.85, 32.45) * mm, "end": v(622.85, 33.21) * mm});
            skLineSegment(sketch, "E1067.MirrorCS", {"start": v(608.43, 33.94) * mm, "end": v(608.44, 33.18) * mm});
            skLineSegment(sketch, "E1068.MirrorCS", {"start": v(563.03, 33.07) * mm, "end": v(563.03, 33.83) * mm});
            skLineSegment(sketch, "E1069.MirrorCS", {"start": v(563.03, 33.07) * mm, "end": v(563.03, 32.3) * mm});
            skLineSegment(sketch, "E1070.MirrorCS", {"start": v(577, 32.34) * mm, "end": v(577, 33.1) * mm});
            skLineSegment(sketch, "E1071.MirrorCS", {"start": v(580.17, 33.11) * mm, "end": v(580.17, 32.35) * mm});
            skLineSegment(sketch, "E1072.MirrorCS", {"start": v(611.61, 33.19) * mm, "end": v(611.6, 33.95) * mm});
            skLineSegment(sketch, "E1073.MirrorCS", {"start": v(593.17, 32.38) * mm, "end": v(593.17, 33.14) * mm});
            skLineSegment(sketch, "E1074.MirrorCS", {"start": v(596.34, 33.15) * mm, "end": v(596.34, 33.91) * mm});
            skLineSegment(sketch, "E1075.MirrorCS", {"start": v(596.34, 33.15) * mm, "end": v(596.35, 32.39) * mm});
            skLineSegment(sketch, "E1076.MirrorCS", {"start": v(577, 33.86) * mm, "end": v(577, 33.1) * mm});
            skLineSegment(sketch, "E1077.MirrorCS", {"start": v(580.17, 33.11) * mm, "end": v(580.17, 33.87) * mm});
            skLineSegment(sketch, "E1078.MirrorCS", {"start": v(608.44, 32.42) * mm, "end": v(608.44, 33.18) * mm});
            skLineSegment(sketch, "E1079.MirrorCS", {"start": v(622.84, 33.98) * mm, "end": v(622.85, 33.21) * mm});
            skLineSegment(sketch, "E1080.MirrorCS", {"start": v(611.61, 33.19) * mm, "end": v(611.61, 32.42) * mm});
            skLineSegment(sketch, "E1081.MirrorCS", {"start": v(593.17, 33.9) * mm, "end": v(593.17, 33.14) * mm});
            skLineSegment(sketch, "E1082.MirrorCS", {"start": v(580.17, 33.87) * mm, "end": v(593.17, 33.9) * mm});
            skLineSegment(sketch, "E1083.MirrorCS", {"start": v(563.03, 33.83) * mm, "end": v(577, 33.86) * mm});
            skLineSegment(sketch, "E1084.MirrorCS", {"start": v(563.03, 32.3) * mm, "end": v(577, 32.34) * mm});
            skLineSegment(sketch, "E1085.MirrorCS", {"start": v(611.6, 33.95) * mm, "end": v(622.84, 33.98) * mm});
            skLineSegment(sketch, "E1086.MirrorCS", {"start": v(596.34, 33.91) * mm, "end": v(608.43, 33.94) * mm});
            skLineSegment(sketch, "E1087.MirrorCS", {"start": v(580.17, 32.35) * mm, "end": v(593.17, 32.38) * mm});
            skLineSegment(sketch, "E1088.MirrorCS", {"start": v(596.35, 32.39) * mm, "end": v(608.44, 32.42) * mm});
            skLineSegment(sketch, "E1089.MirrorCS", {"start": v(611.61, 32.42) * mm, "end": v(622.85, 32.45) * mm});
            skLineSegment(sketch, "E1090.MirrorCS", {"start": v(380.5, 31.87) * mm, "end": v(380.5, 32.63) * mm});
            skSolve(sketch);
        }
        {
            var Q0;
            Q0=qCreatedBy(makeId("Front.planeOp"),FACE);
            var sketch = newSketch(context, id + "F1", { "sketchPlane" : qUnion([Q0])});
            skLineSegment(sketch, "E1091", {"start": v(0, 0) * mm, "end": v(0, 56.39) * mm});
            skLineSegment(sketch, "E1092", {"start": v(0, 56.39) * mm, "end": v(635, 68.83) * mm});
            skLineSegment(sketch, "E1093", {"start": v(635, 68.83) * mm, "end": v(635, -12.45) * mm});
            skLineSegment(sketch, "E1094", {"start": v(635, -12.45) * mm, "end": v(0, 0) * mm});
            skLineSegment(sketch, "E1095", {"start": v(0, 28.2) * mm, "end": v(897.35, 28.2) * mm, "construction": true});
            skSolve(sketch);
        }
        {
            var Q0;
            Q0=qSketchRegion(id+"F1",true);
            extrude(context, id + "F2", {"entities" : qUnion([Q0]), "depth" : 4.76 * mm});
        }
        {
            var Q0;
            Q0=makeQuery(id+"F2.opExtrude","CAP_FACE",FACE,{"disambiguationData":[OSD([sQuery(id+"F1.wireOp",EDGE,"E1091"),sQuery(id+"F1.wireOp",EDGE,"E1092"),sQuery(id+"F1.wireOp",EDGE,"E1093"),sQuery(id+"F1.wireOp",EDGE,"E1094")])],"isStart":false});
            var sketch = newSketch(context, id + "F3", { "sketchPlane" : qUnion([Q0])});
            skLineSegment(sketch, "E1096", {"start": v(0, 28.2) * mm, "end": v(635, 28.2) * mm, "construction": true});
            skSolve(sketch);
        }
        {
            var Q0;
            Q0=qSketchRegion(id+"F0",true);
            extrude(context, id + "F4", {"entities" : qUnion([Q0]), "operationType" : NewBodyOperationType.REMOVE, "endBound" : BoundingType.THROUGH_ALL, "depth" : 25.4 * mm});
        }
        {
            var Q0;
            Q0=makeQuery(id+"F3.imprint","IMPRINT",FACE,{"disambiguationData":[TD([[makeQuery(id+"F3.imprint","IMPRINT",EDGE,{"derivedFrom":makeQuery(id+"F2.opExtrude","CAP_EDGE",EDGE,{"disambiguationData":[OSD([sQuery(id+"F1.wireOp",EDGE,"E1091")])],"isStart":false})}),-1.0]])]});
            var sketch = newSketch(context, id + "F5", { "sketchPlane" : qUnion([Q0])});
            skCircle(sketch, "E1097", {"center": v(97.4, 13.14) * mm, "radius": 1.13 * mm});
            skLineSegment(sketch, "E1098", {"start": v(0, 14.1) * mm, "end": v(635, 7.87) * mm, "construction": true});
            skCircle(sketch, "E1099", {"center": v(3.18, 14.07) * mm, "radius": 1.13 * mm});
            skCircle(sketch, "E1100", {"center": v(181.33, 12.32) * mm, "radius": 1.13 * mm});
            skCircle(sketch, "E1101", {"center": v(290.4, 11.25) * mm, "radius": 1.13 * mm});
            skCircle(sketch, "E1102", {"center": v(409.3, 10.09) * mm, "radius": 1.13 * mm});
            skCircle(sketch, "E1103", {"center": v(524.06, 8.96) * mm, "radius": 1.13 * mm});
            skCircle(sketch, "E1104", {"center": v(624.44, 7.98) * mm, "radius": 1.13 * mm});
            skCircle(sketch, "E1105.MirrorC", {"center": v(97.4, 43.25) * mm, "radius": 1.13 * mm});
            skCircle(sketch, "E1106.MirrorC", {"center": v(3.18, 42.32) * mm, "radius": 1.13 * mm});
            skCircle(sketch, "E1107.MirrorC", {"center": v(181.33, 44.07) * mm, "radius": 1.13 * mm});
            skCircle(sketch, "E1108.MirrorC", {"center": v(290.4, 45.14) * mm, "radius": 1.13 * mm});
            skCircle(sketch, "E1109.MirrorC", {"center": v(409.3, 46.3) * mm, "radius": 1.13 * mm});
            skCircle(sketch, "E1110.MirrorC", {"center": v(524.06, 47.43) * mm, "radius": 1.13 * mm});
            skCircle(sketch, "E1111.MirrorC", {"center": v(624.44, 48.41) * mm, "radius": 1.13 * mm});
            skSolve(sketch);
        }
        {
            var Q0;
            Q0=qSketchRegion(id+"F5",true);
            extrude(context, id + "F6", {"entities" : qUnion([Q0]), "operationType" : NewBodyOperationType.REMOVE, "endBound" : BoundingType.THROUGH_ALL, "depth" : 25.4 * mm});
        }
        {
            assignVariable(context, id + "F7", {"name" : "swheight", "anyValue" : 1 * mm});
        }
        {
            var Q0;
            Q0=qSketchRegion(id+"F5",true);
            extrude(context, id + "F8", {"entities" : qUnion([Q0]), "operationType" : NewBodyOperationType.REMOVE, "endBound" : BoundingType.THROUGH_ALL, "oppositeDirection" : true, "depth" : 25.4 * mm});
        }
        {
            var Q0;
            Q0=makeQuery(id+"F2.opExtrude","CAP_FACE",FACE,{"disambiguationData":[OSD([sQuery(id+"F1.wireOp",EDGE,"E1091"),sQuery(id+"F1.wireOp",EDGE,"E1092"),sQuery(id+"F1.wireOp",EDGE,"E1093"),sQuery(id+"F1.wireOp",EDGE,"E1094")])],"isStart":false});
            var sketch = newSketch(context, id + "F9", { "sketchPlane" : qUnion([Q0])});
            skLineSegment(sketch, "E1112.bottom", {"start": v(7.86, 6.59) * mm, "end": v(14.36, 6.59) * mm});
            skLineSegment(sketch, "E1112.top", {"start": v(7.86, 0.09) * mm, "end": v(14.36, 0.09) * mm});
            skLineSegment(sketch, "E1112.left", {"start": v(7.86, 6.59) * mm, "end": v(7.86, 0.09) * mm});
            skLineSegment(sketch, "E1112.right", {"start": v(14.36, 6.59) * mm, "end": v(14.36, 0.09) * mm});
            skPoint(sketch, "E1112.middle", {"position": v(11.11, 3.34) * mm});
            skLineSegment(sketch, "E1113.bottom", {"start": v(7.86, 13.69) * mm, "end": v(14.36, 13.69) * mm});
            skLineSegment(sketch, "E1113.top", {"start": v(7.86, 7.19) * mm, "end": v(14.36, 7.19) * mm});
            skLineSegment(sketch, "E1113.left", {"start": v(7.86, 13.69) * mm, "end": v(7.86, 7.19) * mm});
            skLineSegment(sketch, "E1113.right", {"start": v(14.36, 13.69) * mm, "end": v(14.36, 7.19) * mm});
            skPoint(sketch, "E1113.middle", {"position": v(11.11, 10.44) * mm});
            skPoint(sketch, "E1113.middle.positionSnap0", {"position": v(11.11, 6.59) * mm});
            skPoint(sketch, "E1113.centerSnap0", {"position": v(11.11, 6.59) * mm});
            skLineSegment(sketch, "E1114", {"start": v(4.77, 3.44) * mm, "end": v(622.77, -6.94) * mm, "construction": true});
            skPoint(sketch, "E1114.startSnap0", {"position": v(4.76, 3.44) * mm});
            skPoint(sketch, "E1114.endSnap0", {"position": v(622.76, -6.94) * mm});
            skLineSegment(sketch, "E1115.bottom", {"start": v(40.46, 6.04) * mm, "end": v(46.96, 6.04) * mm});
            skLineSegment(sketch, "E1115.top", {"start": v(40.46, -0.46) * mm, "end": v(46.96, -0.46) * mm});
            skLineSegment(sketch, "E1115.left", {"start": v(40.46, 6.04) * mm, "end": v(40.46, -0.46) * mm});
            skLineSegment(sketch, "E1115.right", {"start": v(46.96, 6.04) * mm, "end": v(46.96, -0.46) * mm});
            skPoint(sketch, "E1115.middle", {"position": v(43.7, 2.8) * mm});
            skSolve(sketch);
        }
        {
            var Q0;
            Q0=qSketchRegion(id+"F9",true);
            extrude(context, id + "F10", {"entities" : qUnion([Q0]), "operationType" : NewBodyOperationType.REMOVE, "oppositeDirection" : true, "depth" : getVariable(context, 'swheight')});
        }
    });
